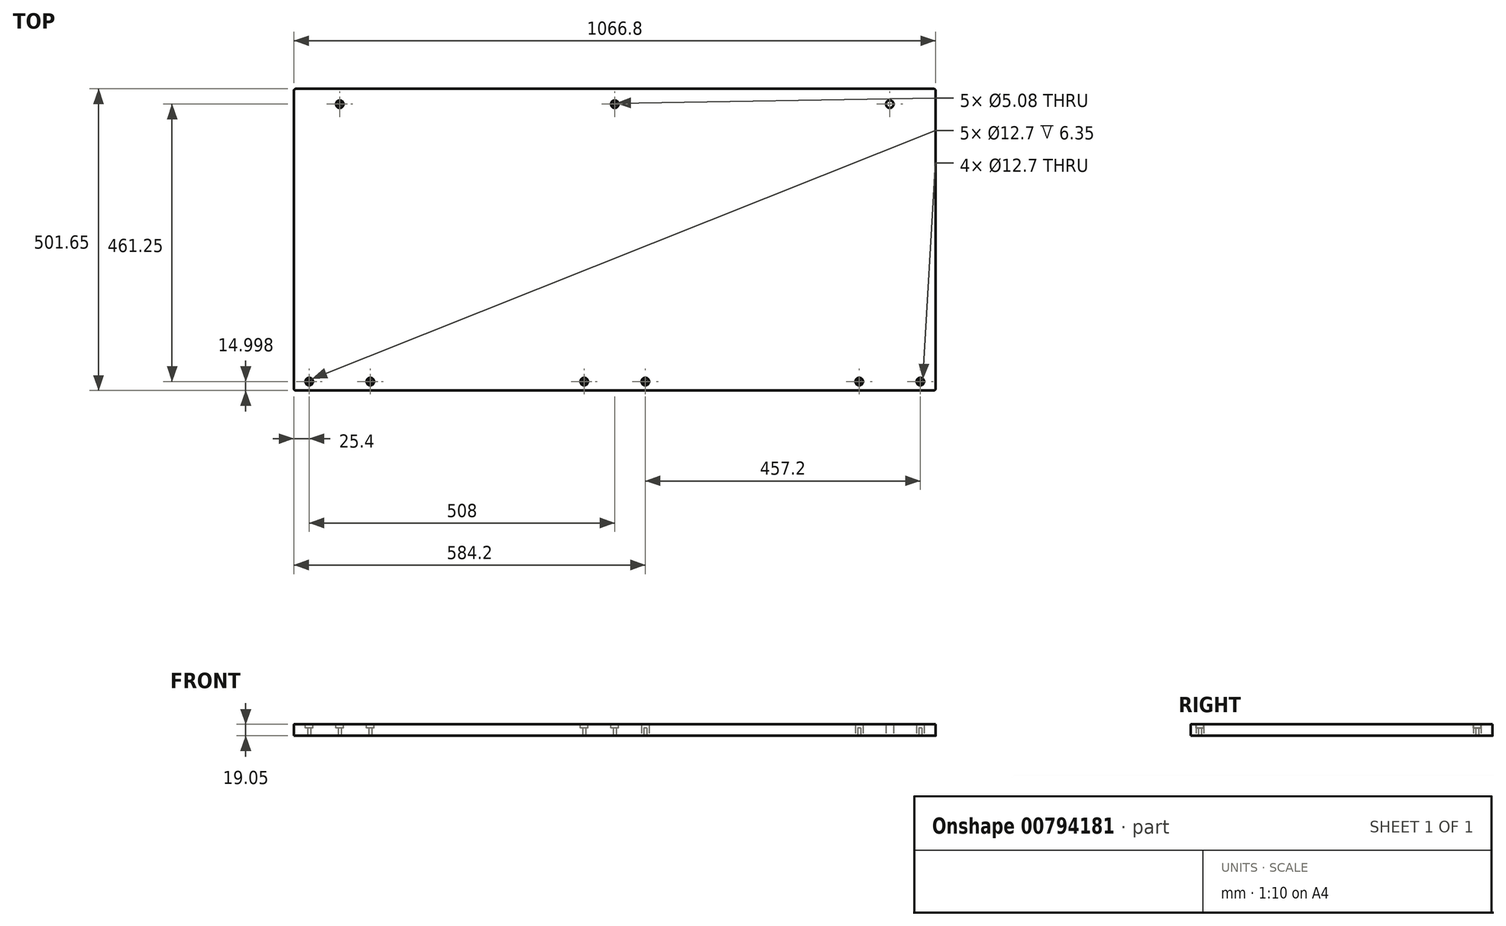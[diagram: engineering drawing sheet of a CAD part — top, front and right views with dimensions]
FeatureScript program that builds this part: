
annotation { "Feature Type Name" : "Feature", "Feature Type Description" : "" }
export const myFeature = defineFeature(function(context is Context, id is Id, definition is map)
    precondition{}
    {
        {
            var Q0;
            Q0=qCreatedBy(makeId("Top.planeOp"),FACE);
            var sketch = newSketch(context, id + "F0", { "sketchPlane" : qUnion([Q0])});
            skFitSpline(sketch, "E0", {"points": [v(-588.01, -204.6) * mm, v(-588.01, -206.35) * mm, v(-586.59, -207.77) * mm, v(-584.84, -207.77) * mm]});
            skFitSpline(sketch, "E1", {"points": [v(475.61, -207.77) * mm, v(477.37, -207.77) * mm, v(478.79, -206.35) * mm, v(478.8, -204.6) * mm]});
            skFitSpline(sketch, "E2", {"points": [v(478.8, 290.7) * mm, v(478.8, 292.46) * mm, v(477.37, 293.88) * mm, v(475.62, 293.88) * mm]});
            skFitSpline(sketch, "E3", {"points": [v(-584.83, 293.88) * mm, v(-586.59, 293.88) * mm, v(-588, 292.46) * mm, v(-588.01, 290.7) * mm]});
            skLineSegment(sketch, "E4", {"start": v(475.49, -207.77) * mm, "end": v(-584.96, -207.77) * mm});
            skLineSegment(sketch, "E5", {"start": v(478.8, 290.58) * mm, "end": v(478.8, -204.72) * mm});
            skLineSegment(sketch, "E6", {"start": v(-584.96, 293.88) * mm, "end": v(475.49, 293.88) * mm});
            skLineSegment(sketch, "E7", {"start": v(-588.01, -204.72) * mm, "end": v(-588.01, 290.58) * mm});
            skLineSegment(sketch, "E8", {"start": v(768.1, -204.72) * mm, "end": v(768.1, -207.77) * mm});
            skLineSegment(sketch, "E9", {"start": v(768.1, 293.88) * mm, "end": v(768.1, 290.58) * mm});
            skLineSegment(sketch, "E10", {"start": v(768.1, -207.77) * mm, "end": v(787.15, -207.77) * mm});
            skLineSegment(sketch, "E11", {"start": v(787.15, -207.77) * mm, "end": v(787.15, -204.72) * mm});
            skLineSegment(sketch, "E12", {"start": v(787.15, 290.58) * mm, "end": v(787.15, 293.88) * mm});
            skLineSegment(sketch, "E13", {"start": v(787.15, 293.88) * mm, "end": v(768.1, 293.88) * mm});
            skLineSegment(sketch, "E14", {"start": v(768.1, 290.58) * mm, "end": v(768.1, -204.72) * mm});
            skLineSegment(sketch, "E15", {"start": v(787.15, 290.58) * mm, "end": v(787.15, -204.72) * mm});
            skLineSegment(sketch, "E16", {"start": v(774.45, -199.14) * mm, "end": v(774.45, -195.07) * mm});
            skLineSegment(sketch, "E17", {"start": v(774.45, -190.75) * mm, "end": v(774.45, -186.44) * mm});
            skLineSegment(sketch, "E18", {"start": v(774.45, 262.13) * mm, "end": v(774.45, 266.2) * mm});
            skLineSegment(sketch, "E19", {"start": v(774.45, 270.51) * mm, "end": v(774.45, 274.83) * mm});
            skLineSegment(sketch, "E20", {"start": v(774.45, -199.14) * mm, "end": v(772.41, -199.14) * mm});
            skLineSegment(sketch, "E21", {"start": v(770.38, -199.14) * mm, "end": v(768.1, -199.14) * mm});
            skLineSegment(sketch, "E22", {"start": v(774.45, -186.44) * mm, "end": v(772.41, -186.44) * mm});
            skLineSegment(sketch, "E23", {"start": v(770.38, -186.44) * mm, "end": v(768.1, -186.44) * mm});
            skLineSegment(sketch, "E24", {"start": v(787.15, -195.33) * mm, "end": v(783.08, -195.33) * mm});
            skLineSegment(sketch, "E25", {"start": v(778.76, -195.33) * mm, "end": v(774.45, -195.33) * mm});
            skLineSegment(sketch, "E26", {"start": v(787.15, -190.25) * mm, "end": v(783.08, -190.25) * mm});
            skLineSegment(sketch, "E27", {"start": v(778.76, -190.25) * mm, "end": v(774.45, -190.25) * mm});
            skLineSegment(sketch, "E28", {"start": v(774.45, 262.13) * mm, "end": v(772.41, 262.13) * mm});
            skLineSegment(sketch, "E29", {"start": v(770.38, 262.13) * mm, "end": v(768.1, 262.13) * mm});
            skLineSegment(sketch, "E30", {"start": v(774.45, 274.83) * mm, "end": v(772.41, 274.83) * mm});
            skLineSegment(sketch, "E31", {"start": v(770.38, 274.83) * mm, "end": v(768.1, 274.83) * mm});
            skLineSegment(sketch, "E32", {"start": v(787.15, 265.94) * mm, "end": v(783.08, 265.94) * mm});
            skLineSegment(sketch, "E33", {"start": v(778.76, 265.94) * mm, "end": v(774.45, 265.94) * mm});
            skLineSegment(sketch, "E34", {"start": v(787.15, 271.02) * mm, "end": v(783.08, 271.02) * mm});
            skLineSegment(sketch, "E35", {"start": v(778.76, 271.02) * mm, "end": v(774.45, 271.02) * mm});
            skLineSegment(sketch, "E36", {"start": v(-1041.4, -812.8) * mm, "end": v(-1041.4, 812.8) * mm});
            skLineSegment(sketch, "E37", {"start": v(-1041.4, 812.8) * mm, "end": v(1041.4, 812.8) * mm});
            skLineSegment(sketch, "E38", {"start": v(1041.4, 812.8) * mm, "end": v(1041.4, -812.8) * mm});
            skLineSegment(sketch, "E39", {"start": v(1041.4, -812.8) * mm, "end": v(-1041.4, -812.8) * mm});
            skLineSegment(sketch, "E40", {"start": v(0, -838.2) * mm, "end": v(0, -812.8) * mm});
            skLineSegment(sketch, "E41", {"start": v(0, -812.8) * mm, "end": v(-8.89, -828.04) * mm});
            skLineSegment(sketch, "E42", {"start": v(-8.89, -828.04) * mm, "end": v(8.89, -828.04) * mm});
            skLineSegment(sketch, "E43", {"start": v(8.89, -828.04) * mm, "end": v(0, -812.8) * mm});
            skLineSegment(sketch, "E44", {"start": v(0, 838.2) * mm, "end": v(0, 812.8) * mm});
            skLineSegment(sketch, "E45", {"start": v(0, 812.8) * mm, "end": v(-8.89, 828.04) * mm});
            skLineSegment(sketch, "E46", {"start": v(-8.89, 828.04) * mm, "end": v(8.89, 828.04) * mm});
            skLineSegment(sketch, "E47", {"start": v(8.89, 828.04) * mm, "end": v(0, 812.8) * mm});
            skLineSegment(sketch, "E48", {"start": v(-1066.8, 0) * mm, "end": v(-1041.4, 0) * mm});
            skLineSegment(sketch, "E49", {"start": v(-1041.4, 0) * mm, "end": v(-1056.64, 8.89) * mm});
            skLineSegment(sketch, "E50", {"start": v(-1056.64, 8.89) * mm, "end": v(-1056.64, -8.89) * mm});
            skLineSegment(sketch, "E51", {"start": v(-1056.64, -8.89) * mm, "end": v(-1041.4, 0) * mm});
            skLineSegment(sketch, "E52", {"start": v(1066.8, 0) * mm, "end": v(1041.4, 0) * mm});
            skLineSegment(sketch, "E53", {"start": v(1041.4, 0) * mm, "end": v(1056.64, 8.89) * mm});
            skLineSegment(sketch, "E54", {"start": v(1056.64, 8.89) * mm, "end": v(1056.64, -8.89) * mm});
            skLineSegment(sketch, "E55", {"start": v(1056.64, -8.89) * mm, "end": v(1041.4, 0) * mm});
            skLineSegment(sketch, "E56", {"start": v(-558.8, -812.8) * mm, "end": v(-558.8, -829.06) * mm});
            skLineSegment(sketch, "E57", {"start": v(-558.8, 812.8) * mm, "end": v(-558.8, 829.06) * mm});
            skLineSegment(sketch, "E58", {"start": v(558.8, -812.8) * mm, "end": v(558.8, -829.06) * mm});
            skLineSegment(sketch, "E59", {"start": v(558.8, 812.8) * mm, "end": v(558.8, 829.06) * mm});
            skLineSegment(sketch, "E60", {"start": v(-834.04, 821.05) * mm, "end": v(-835.49, 821.05) * mm});
            skLineSegment(sketch, "E61", {"start": v(-835.49, 821.05) * mm, "end": v(-835.49, 816.86) * mm});
            skLineSegment(sketch, "E62", {"start": v(-835.49, 816.86) * mm, "end": v(-837.06, 816.86) * mm});
            skLineSegment(sketch, "E63", {"start": v(-837.06, 816.86) * mm, "end": v(-837.06, 821.05) * mm});
            skLineSegment(sketch, "E64", {"start": v(-837.06, 821.05) * mm, "end": v(-842.44, 821.05) * mm});
            skLineSegment(sketch, "E65", {"start": v(-842.44, 821.05) * mm, "end": v(-842.44, 822.77) * mm});
            skLineSegment(sketch, "E66", {"start": v(-842.44, 822.77) * mm, "end": v(-837, 829.05) * mm});
            skLineSegment(sketch, "E67", {"start": v(-837, 829.05) * mm, "end": v(-835.49, 829.05) * mm});
            skLineSegment(sketch, "E68", {"start": v(-835.49, 829.05) * mm, "end": v(-835.49, 822.36) * mm});
            skLineSegment(sketch, "E69", {"start": v(-835.49, 822.36) * mm, "end": v(-834.04, 822.36) * mm});
            skLineSegment(sketch, "E70", {"start": v(-834.04, 822.36) * mm, "end": v(-834.04, 821.05) * mm});
            skLineSegment(sketch, "E71", {"start": v(-837.06, 822.36) * mm, "end": v(-837.06, 827.13) * mm});
            skLineSegment(sketch, "E72", {"start": v(-837.06, 827.13) * mm, "end": v(-841.17, 822.36) * mm});
            skLineSegment(sketch, "E73", {"start": v(-841.17, 822.36) * mm, "end": v(-837.06, 822.36) * mm});
            skLineSegment(sketch, "E74", {"start": v(-834.04, -824.86) * mm, "end": v(-835.49, -824.86) * mm});
            skLineSegment(sketch, "E75", {"start": v(-835.49, -824.86) * mm, "end": v(-835.49, -829.06) * mm});
            skLineSegment(sketch, "E76", {"start": v(-835.49, -829.06) * mm, "end": v(-837.06, -829.06) * mm});
            skLineSegment(sketch, "E77", {"start": v(-837.06, -829.06) * mm, "end": v(-837.06, -824.86) * mm});
            skLineSegment(sketch, "E78", {"start": v(-837.06, -824.86) * mm, "end": v(-842.44, -824.86) * mm});
            skLineSegment(sketch, "E79", {"start": v(-842.44, -824.86) * mm, "end": v(-842.44, -823.15) * mm});
            skLineSegment(sketch, "E80", {"start": v(-842.44, -823.15) * mm, "end": v(-837, -816.87) * mm});
            skLineSegment(sketch, "E81", {"start": v(-837, -816.87) * mm, "end": v(-835.49, -816.87) * mm});
            skLineSegment(sketch, "E82", {"start": v(-835.49, -816.87) * mm, "end": v(-835.49, -823.55) * mm});
            skLineSegment(sketch, "E83", {"start": v(-835.49, -823.55) * mm, "end": v(-834.04, -823.55) * mm});
            skLineSegment(sketch, "E84", {"start": v(-834.04, -823.55) * mm, "end": v(-834.04, -824.86) * mm});
            skLineSegment(sketch, "E85", {"start": v(-837.06, -823.55) * mm, "end": v(-837.06, -818.8) * mm});
            skLineSegment(sketch, "E86", {"start": v(-837.06, -818.8) * mm, "end": v(-841.17, -823.55) * mm});
            skLineSegment(sketch, "E87", {"start": v(-841.17, -823.55) * mm, "end": v(-837.06, -823.55) * mm});
            skLineSegment(sketch, "E88", {"start": v(-1041.4, -431.8) * mm, "end": v(-1057.66, -431.8) * mm});
            skLineSegment(sketch, "E89", {"start": v(1041.4, -431.8) * mm, "end": v(1057.66, -431.8) * mm});
            skLineSegment(sketch, "E90", {"start": v(-1041.4, 431.8) * mm, "end": v(-1057.66, 431.8) * mm});
            skLineSegment(sketch, "E91", {"start": v(1041.4, 431.8) * mm, "end": v(1057.66, 431.8) * mm});
            skLineSegment(sketch, "E92", {"start": v(-1056.72, -653.8) * mm, "end": v(-1052.61, -641.6) * mm});
            skLineSegment(sketch, "E93", {"start": v(-1052.61, -641.6) * mm, "end": v(-1050.62, -641.6) * mm});
            skLineSegment(sketch, "E94", {"start": v(-1050.62, -641.6) * mm, "end": v(-1046.5, -653.8) * mm});
            skLineSegment(sketch, "E95", {"start": v(-1046.5, -653.8) * mm, "end": v(-1048.22, -653.8) * mm});
            skLineSegment(sketch, "E96", {"start": v(-1048.22, -653.8) * mm, "end": v(-1049.32, -650.4) * mm});
            skLineSegment(sketch, "E97", {"start": v(-1049.32, -650.4) * mm, "end": v(-1053.98, -650.4) * mm});
            skLineSegment(sketch, "E98", {"start": v(-1053.98, -650.4) * mm, "end": v(-1055.08, -653.8) * mm});
            skLineSegment(sketch, "E99", {"start": v(-1055.08, -653.8) * mm, "end": v(-1056.72, -653.8) * mm});
            skLineSegment(sketch, "E100", {"start": v(-1049.77, -649) * mm, "end": v(-1051.65, -643.26) * mm});
            skLineSegment(sketch, "E101", {"start": v(-1051.65, -643.26) * mm, "end": v(-1053.53, -649) * mm});
            skLineSegment(sketch, "E102", {"start": v(-1053.53, -649) * mm, "end": v(-1049.77, -649) * mm});
            skLineSegment(sketch, "E103", {"start": v(1046.4, -653.8) * mm, "end": v(1050.5, -641.6) * mm});
            skLineSegment(sketch, "E104", {"start": v(1050.5, -641.6) * mm, "end": v(1052.5, -641.6) * mm});
            skLineSegment(sketch, "E105", {"start": v(1052.5, -641.6) * mm, "end": v(1056.61, -653.8) * mm});
            skLineSegment(sketch, "E106", {"start": v(1056.61, -653.8) * mm, "end": v(1054.9, -653.8) * mm});
            skLineSegment(sketch, "E107", {"start": v(1054.9, -653.8) * mm, "end": v(1053.8, -650.4) * mm});
            skLineSegment(sketch, "E108", {"start": v(1053.8, -650.4) * mm, "end": v(1049.14, -650.4) * mm});
            skLineSegment(sketch, "E109", {"start": v(1049.14, -650.4) * mm, "end": v(1048.03, -653.8) * mm});
            skLineSegment(sketch, "E110", {"start": v(1048.03, -653.8) * mm, "end": v(1046.4, -653.8) * mm});
            skLineSegment(sketch, "E111", {"start": v(1053.35, -649) * mm, "end": v(1051.46, -643.26) * mm});
            skLineSegment(sketch, "E112", {"start": v(1051.46, -643.26) * mm, "end": v(1049.6, -649) * mm});
            skLineSegment(sketch, "E113", {"start": v(1049.6, -649) * mm, "end": v(1053.35, -649) * mm});
            skLineSegment(sketch, "E114", {"start": v(254, -596.9) * mm, "end": v(533.4, -596.9) * mm});
            skLineSegment(sketch, "E115", {"start": v(254, -635) * mm, "end": v(533.4, -635) * mm});
            skLineSegment(sketch, "E116", {"start": v(254, -673.1) * mm, "end": v(533.4, -673.1) * mm});
            skLineSegment(sketch, "E117", {"start": v(254, -711.2) * mm, "end": v(533.4, -711.2) * mm});
            skLineSegment(sketch, "E118", {"start": v(254, -749.3) * mm, "end": v(533.4, -749.3) * mm});
            skLineSegment(sketch, "E119", {"start": v(431.8, -812.8) * mm, "end": v(431.8, -558.8) * mm});
            skLineSegment(sketch, "E120", {"start": v(990.6, -787.4) * mm, "end": v(990.6, -736.6) * mm});
            skLineSegment(sketch, "E121", {"start": v(838.2, -787.4) * mm, "end": v(838.2, -812.8) * mm});
            skLineSegment(sketch, "E122", {"start": v(685.8, -787.4) * mm, "end": v(685.8, -736.6) * mm});
            skLineSegment(sketch, "E123", {"start": v(647.2, -787.4) * mm, "end": v(647.2, -812.8) * mm});
            skLineSegment(sketch, "E124", {"start": v(584.2, -787.4) * mm, "end": v(584.2, -736.6) * mm});
            skLineSegment(sketch, "E125", {"start": v(1041.4, -787.4) * mm, "end": v(533.4, -787.4) * mm});
            skLineSegment(sketch, "E126", {"start": v(533.4, -787.4) * mm, "end": v(254, -787.4) * mm});
            skLineSegment(sketch, "E127", {"start": v(1041.4, -736.6) * mm, "end": v(533.4, -736.6) * mm});
            skLineSegment(sketch, "E128", {"start": v(533.4, -621.8) * mm, "end": v(1041.4, -621.8) * mm});
            skLineSegment(sketch, "E129", {"start": v(533.4, -812.8) * mm, "end": v(533.4, -558.8) * mm});
            skLineSegment(sketch, "E130", {"start": v(254, -812.8) * mm, "end": v(1041.4, -812.8) * mm});
            skLineSegment(sketch, "E131", {"start": v(1041.4, -812.8) * mm, "end": v(1041.4, -558.8) * mm});
            skLineSegment(sketch, "E132", {"start": v(1041.4, -558.8) * mm, "end": v(254, -558.8) * mm});
            skLineSegment(sketch, "E133", {"start": v(254, -558.8) * mm, "end": v(254, -812.8) * mm});
            skLineSegment(sketch, "E134", {"start": v(857.53, -809.5) * mm, "end": v(856.18, -809.5) * mm});
            skLineSegment(sketch, "E135", {"start": v(856.18, -809.5) * mm, "end": v(856.18, -804.53) * mm});
            skLineSegment(sketch, "E136", {"start": v(856.18, -804.53) * mm, "end": v(851.5, -804.53) * mm});
            skLineSegment(sketch, "E137", {"start": v(851.5, -804.53) * mm, "end": v(851.5, -809.5) * mm});
            skLineSegment(sketch, "E138", {"start": v(851.5, -809.5) * mm, "end": v(850.15, -809.5) * mm});
            skLineSegment(sketch, "E139", {"start": v(850.15, -809.5) * mm, "end": v(850.15, -799.34) * mm});
            skLineSegment(sketch, "E140", {"start": v(850.15, -799.34) * mm, "end": v(851.5, -799.34) * mm});
            skLineSegment(sketch, "E141", {"start": v(851.5, -799.34) * mm, "end": v(851.5, -803.32) * mm});
            skLineSegment(sketch, "E142", {"start": v(851.5, -803.32) * mm, "end": v(856.18, -803.32) * mm});
            skLineSegment(sketch, "E143", {"start": v(856.18, -803.32) * mm, "end": v(856.18, -799.34) * mm});
            skLineSegment(sketch, "E144", {"start": v(856.18, -799.34) * mm, "end": v(857.53, -799.34) * mm});
            skLineSegment(sketch, "E145", {"start": v(857.53, -799.34) * mm, "end": v(857.53, -809.5) * mm});
            skLineSegment(sketch, "E146", {"start": v(859.55, -809.5) * mm, "end": v(859.55, -799.34) * mm});
            skLineSegment(sketch, "E147", {"start": v(859.55, -799.34) * mm, "end": v(865.9, -799.34) * mm});
            skLineSegment(sketch, "E148", {"start": v(865.9, -799.34) * mm, "end": v(865.9, -800.54) * mm});
            skLineSegment(sketch, "E149", {"start": v(865.9, -800.54) * mm, "end": v(860.9, -800.54) * mm});
            skLineSegment(sketch, "E150", {"start": v(860.9, -800.54) * mm, "end": v(860.9, -803.32) * mm});
            skLineSegment(sketch, "E151", {"start": v(860.9, -803.32) * mm, "end": v(865.56, -803.32) * mm});
            skLineSegment(sketch, "E152", {"start": v(865.56, -803.32) * mm, "end": v(865.56, -804.53) * mm});
            skLineSegment(sketch, "E153", {"start": v(865.56, -804.53) * mm, "end": v(860.9, -804.53) * mm});
            skLineSegment(sketch, "E154", {"start": v(860.9, -804.53) * mm, "end": v(860.9, -808.3) * mm});
            skLineSegment(sketch, "E155", {"start": v(860.9, -808.3) * mm, "end": v(865.9, -808.3) * mm});
            skLineSegment(sketch, "E156", {"start": v(865.9, -808.3) * mm, "end": v(865.9, -809.5) * mm});
            skLineSegment(sketch, "E157", {"start": v(865.9, -809.5) * mm, "end": v(859.55, -809.5) * mm});
            skLineSegment(sketch, "E158", {"start": v(867.42, -809.5) * mm, "end": v(867.42, -799.34) * mm});
            skLineSegment(sketch, "E159", {"start": v(867.42, -799.34) * mm, "end": v(873.78, -799.34) * mm});
            skLineSegment(sketch, "E160", {"start": v(873.78, -799.34) * mm, "end": v(873.78, -800.54) * mm});
            skLineSegment(sketch, "E161", {"start": v(873.78, -800.54) * mm, "end": v(868.78, -800.54) * mm});
            skLineSegment(sketch, "E162", {"start": v(868.78, -800.54) * mm, "end": v(868.78, -803.32) * mm});
            skLineSegment(sketch, "E163", {"start": v(868.78, -803.32) * mm, "end": v(873.43, -803.32) * mm});
            skLineSegment(sketch, "E164", {"start": v(873.43, -803.32) * mm, "end": v(873.43, -804.53) * mm});
            skLineSegment(sketch, "E165", {"start": v(873.43, -804.53) * mm, "end": v(868.78, -804.53) * mm});
            skLineSegment(sketch, "E166", {"start": v(868.78, -804.53) * mm, "end": v(868.78, -808.3) * mm});
            skLineSegment(sketch, "E167", {"start": v(868.78, -808.3) * mm, "end": v(873.78, -808.3) * mm});
            skLineSegment(sketch, "E168", {"start": v(873.78, -808.3) * mm, "end": v(873.78, -809.5) * mm});
            skLineSegment(sketch, "E169", {"start": v(873.78, -809.5) * mm, "end": v(867.42, -809.5) * mm});
            skLineSegment(sketch, "E170", {"start": v(877.42, -809.5) * mm, "end": v(877.42, -800.54) * mm});
            skLineSegment(sketch, "E171", {"start": v(877.42, -800.54) * mm, "end": v(874, -800.54) * mm});
            skLineSegment(sketch, "E172", {"start": v(874, -800.54) * mm, "end": v(874, -799.34) * mm});
            skLineSegment(sketch, "E173", {"start": v(874, -799.34) * mm, "end": v(882.18, -799.34) * mm});
            skLineSegment(sketch, "E174", {"start": v(882.18, -799.34) * mm, "end": v(882.18, -800.54) * mm});
            skLineSegment(sketch, "E175", {"start": v(882.18, -800.54) * mm, "end": v(878.77, -800.54) * mm});
            skLineSegment(sketch, "E176", {"start": v(878.77, -800.54) * mm, "end": v(878.77, -809.5) * mm});
            skLineSegment(sketch, "E177", {"start": v(878.77, -809.5) * mm, "end": v(877.42, -809.5) * mm});
            skLineSegment(sketch, "E178", {"start": v(924.05, -800.54) * mm, "end": v(919.32, -800.54) * mm});
            skLineSegment(sketch, "E179", {"start": v(919.32, -800.54) * mm, "end": v(919.32, -803.4) * mm});
            skLineSegment(sketch, "E180", {"start": v(919.32, -803.4) * mm, "end": v(923.85, -803.4) * mm});
            skLineSegment(sketch, "E181", {"start": v(923.85, -803.4) * mm, "end": v(923.85, -804.6) * mm});
            skLineSegment(sketch, "E182", {"start": v(923.85, -804.6) * mm, "end": v(919.32, -804.6) * mm});
            skLineSegment(sketch, "E183", {"start": v(919.32, -804.6) * mm, "end": v(919.32, -809.5) * mm});
            skLineSegment(sketch, "E184", {"start": v(919.32, -809.5) * mm, "end": v(917.97, -809.5) * mm});
            skLineSegment(sketch, "E185", {"start": v(917.97, -809.5) * mm, "end": v(917.97, -799.34) * mm});
            skLineSegment(sketch, "E186", {"start": v(917.97, -799.34) * mm, "end": v(924.05, -799.34) * mm});
            skLineSegment(sketch, "E187", {"start": v(924.05, -799.34) * mm, "end": v(924.05, -800.54) * mm});
            skLineSegment(sketch, "E188", {"start": v(275.01, -572) * mm, "end": v(278.44, -561.85) * mm});
            skLineSegment(sketch, "E189", {"start": v(278.44, -561.85) * mm, "end": v(280.1, -561.85) * mm});
            skLineSegment(sketch, "E190", {"start": v(280.1, -561.85) * mm, "end": v(283.53, -572) * mm});
            skLineSegment(sketch, "E191", {"start": v(283.53, -572) * mm, "end": v(282.1, -572) * mm});
            skLineSegment(sketch, "E192", {"start": v(282.1, -572) * mm, "end": v(281.18, -569.17) * mm});
            skLineSegment(sketch, "E193", {"start": v(281.18, -569.17) * mm, "end": v(277.3, -569.17) * mm});
            skLineSegment(sketch, "E194", {"start": v(277.3, -569.17) * mm, "end": v(276.38, -572) * mm});
            skLineSegment(sketch, "E195", {"start": v(276.38, -572) * mm, "end": v(275.01, -572) * mm});
            skLineSegment(sketch, "E196", {"start": v(280.8, -568.02) * mm, "end": v(279.24, -563.23) * mm});
            skLineSegment(sketch, "E197", {"start": v(279.24, -563.23) * mm, "end": v(277.67, -568.02) * mm});
            skLineSegment(sketch, "E198", {"start": v(277.67, -568.02) * mm, "end": v(280.8, -568.02) * mm});
            skLineSegment(sketch, "E199", {"start": v(295.89, -561.85) * mm, "end": v(293.33, -572) * mm});
            skLineSegment(sketch, "E200", {"start": v(293.33, -572) * mm, "end": v(291.81, -572) * mm});
            skLineSegment(sketch, "E201", {"start": v(291.81, -572) * mm, "end": v(289.75, -563.58) * mm});
            skLineSegment(sketch, "E202", {"start": v(289.75, -563.58) * mm, "end": v(287.73, -572) * mm});
            skLineSegment(sketch, "E203", {"start": v(287.73, -572) * mm, "end": v(286.24, -572) * mm});
            skLineSegment(sketch, "E204", {"start": v(286.24, -572) * mm, "end": v(283.64, -561.85) * mm});
            skLineSegment(sketch, "E205", {"start": v(283.64, -561.85) * mm, "end": v(285.03, -561.85) * mm});
            skLineSegment(sketch, "E206", {"start": v(285.03, -561.85) * mm, "end": v(287.07, -570.3) * mm});
            skLineSegment(sketch, "E207", {"start": v(287.07, -570.3) * mm, "end": v(289.1, -561.85) * mm});
            skLineSegment(sketch, "E208", {"start": v(289.1, -561.85) * mm, "end": v(290.48, -561.85) * mm});
            skLineSegment(sketch, "E209", {"start": v(290.48, -561.85) * mm, "end": v(292.53, -570.38) * mm});
            skLineSegment(sketch, "E210", {"start": v(292.53, -570.38) * mm, "end": v(294.56, -561.85) * mm});
            skLineSegment(sketch, "E211", {"start": v(294.56, -561.85) * mm, "end": v(295.89, -561.85) * mm});
            skLineSegment(sketch, "E212", {"start": v(304.46, -572) * mm, "end": v(302.94, -572) * mm});
            skLineSegment(sketch, "E213", {"start": v(302.94, -572) * mm, "end": v(298.46, -563.25) * mm});
            skLineSegment(sketch, "E214", {"start": v(298.46, -563.25) * mm, "end": v(298.46, -572) * mm});
            skLineSegment(sketch, "E215", {"start": v(298.46, -572) * mm, "end": v(297.2, -572) * mm});
            skLineSegment(sketch, "E216", {"start": v(297.2, -572) * mm, "end": v(297.2, -561.85) * mm});
            skLineSegment(sketch, "E217", {"start": v(297.2, -561.85) * mm, "end": v(299.11, -561.85) * mm});
            skLineSegment(sketch, "E218", {"start": v(299.11, -561.85) * mm, "end": v(303.2, -569.9) * mm});
            skLineSegment(sketch, "E219", {"start": v(303.2, -569.9) * mm, "end": v(303.2, -561.85) * mm});
            skLineSegment(sketch, "E220", {"start": v(303.2, -561.85) * mm, "end": v(304.46, -561.85) * mm});
            skLineSegment(sketch, "E221", {"start": v(304.46, -561.85) * mm, "end": v(304.46, -572) * mm});
            skLineSegment(sketch, "E222", {"start": v(273.83, -610.36) * mm, "end": v(272.48, -610.36) * mm});
            skLineSegment(sketch, "E223", {"start": v(272.48, -610.36) * mm, "end": v(272.48, -605.39) * mm});
            skLineSegment(sketch, "E224", {"start": v(272.48, -605.39) * mm, "end": v(267.81, -605.39) * mm});
            skLineSegment(sketch, "E225", {"start": v(267.81, -605.39) * mm, "end": v(267.81, -610.36) * mm});
            skLineSegment(sketch, "E226", {"start": v(267.81, -610.36) * mm, "end": v(266.46, -610.36) * mm});
            skLineSegment(sketch, "E227", {"start": v(266.46, -610.36) * mm, "end": v(266.46, -600.2) * mm});
            skLineSegment(sketch, "E228", {"start": v(266.46, -600.2) * mm, "end": v(267.81, -600.2) * mm});
            skLineSegment(sketch, "E229", {"start": v(267.81, -600.2) * mm, "end": v(267.81, -604.19) * mm});
            skLineSegment(sketch, "E230", {"start": v(267.81, -604.19) * mm, "end": v(272.48, -604.19) * mm});
            skLineSegment(sketch, "E231", {"start": v(272.48, -604.19) * mm, "end": v(272.48, -600.2) * mm});
            skLineSegment(sketch, "E232", {"start": v(272.48, -600.2) * mm, "end": v(273.83, -600.2) * mm});
            skLineSegment(sketch, "E233", {"start": v(273.83, -600.2) * mm, "end": v(273.83, -610.36) * mm});
            skLineSegment(sketch, "E234", {"start": v(275.86, -610.36) * mm, "end": v(275.86, -600.2) * mm});
            skLineSegment(sketch, "E235", {"start": v(275.86, -600.2) * mm, "end": v(282.2, -600.2) * mm});
            skLineSegment(sketch, "E236", {"start": v(282.2, -600.2) * mm, "end": v(282.2, -601.4) * mm});
            skLineSegment(sketch, "E237", {"start": v(282.2, -601.4) * mm, "end": v(277.2, -601.4) * mm});
            skLineSegment(sketch, "E238", {"start": v(277.2, -601.4) * mm, "end": v(277.2, -604.19) * mm});
            skLineSegment(sketch, "E239", {"start": v(277.2, -604.19) * mm, "end": v(281.87, -604.19) * mm});
            skLineSegment(sketch, "E240", {"start": v(281.87, -604.19) * mm, "end": v(281.87, -605.39) * mm});
            skLineSegment(sketch, "E241", {"start": v(281.87, -605.39) * mm, "end": v(277.2, -605.39) * mm});
            skLineSegment(sketch, "E242", {"start": v(277.2, -605.39) * mm, "end": v(277.2, -609.16) * mm});
            skLineSegment(sketch, "E243", {"start": v(277.2, -609.16) * mm, "end": v(282.2, -609.16) * mm});
            skLineSegment(sketch, "E244", {"start": v(282.2, -609.16) * mm, "end": v(282.2, -610.36) * mm});
            skLineSegment(sketch, "E245", {"start": v(282.2, -610.36) * mm, "end": v(275.86, -610.36) * mm});
            skLineSegment(sketch, "E246", {"start": v(299.52, -610.36) * mm, "end": v(297.76, -610.36) * mm});
            skLineSegment(sketch, "E247", {"start": v(297.76, -610.36) * mm, "end": v(294.06, -605.64) * mm});
            skLineSegment(sketch, "E248", {"start": v(294.06, -605.64) * mm, "end": v(293.46, -606.3) * mm});
            skLineSegment(sketch, "E249", {"start": v(293.46, -606.3) * mm, "end": v(293.46, -610.36) * mm});
            skLineSegment(sketch, "E250", {"start": v(293.46, -610.36) * mm, "end": v(292.11, -610.36) * mm});
            skLineSegment(sketch, "E251", {"start": v(292.11, -610.36) * mm, "end": v(292.11, -600.2) * mm});
            skLineSegment(sketch, "E252", {"start": v(292.11, -600.2) * mm, "end": v(293.46, -600.2) * mm});
            skLineSegment(sketch, "E253", {"start": v(293.46, -600.2) * mm, "end": v(293.46, -604.88) * mm});
            skLineSegment(sketch, "E254", {"start": v(293.46, -604.88) * mm, "end": v(297.63, -600.2) * mm});
            skLineSegment(sketch, "E255", {"start": v(297.63, -600.2) * mm, "end": v(299.27, -600.2) * mm});
            skLineSegment(sketch, "E256", {"start": v(299.27, -600.2) * mm, "end": v(295.07, -604.74) * mm});
            skLineSegment(sketch, "E257", {"start": v(295.07, -604.74) * mm, "end": v(299.52, -610.36) * mm});
            skLineSegment(sketch, "E258", {"start": v(300.24, -610.36) * mm, "end": v(300.24, -600.2) * mm});
            skLineSegment(sketch, "E259", {"start": v(300.24, -600.2) * mm, "end": v(306.6, -600.2) * mm});
            skLineSegment(sketch, "E260", {"start": v(306.6, -600.2) * mm, "end": v(306.6, -601.4) * mm});
            skLineSegment(sketch, "E261", {"start": v(306.6, -601.4) * mm, "end": v(301.6, -601.4) * mm});
            skLineSegment(sketch, "E262", {"start": v(301.6, -601.4) * mm, "end": v(301.6, -604.19) * mm});
            skLineSegment(sketch, "E263", {"start": v(301.6, -604.19) * mm, "end": v(306.25, -604.19) * mm});
            skLineSegment(sketch, "E264", {"start": v(306.25, -604.19) * mm, "end": v(306.25, -605.39) * mm});
            skLineSegment(sketch, "E265", {"start": v(306.25, -605.39) * mm, "end": v(301.6, -605.39) * mm});
            skLineSegment(sketch, "E266", {"start": v(301.6, -605.39) * mm, "end": v(301.6, -609.16) * mm});
            skLineSegment(sketch, "E267", {"start": v(301.6, -609.16) * mm, "end": v(306.6, -609.16) * mm});
            skLineSegment(sketch, "E268", {"start": v(306.6, -609.16) * mm, "end": v(306.6, -610.36) * mm});
            skLineSegment(sketch, "E269", {"start": v(306.6, -610.36) * mm, "end": v(300.24, -610.36) * mm});
            skLineSegment(sketch, "E270", {"start": v(266.89, -648.46) * mm, "end": v(270.3, -638.3) * mm});
            skLineSegment(sketch, "E271", {"start": v(270.3, -638.3) * mm, "end": v(271.97, -638.3) * mm});
            skLineSegment(sketch, "E272", {"start": v(271.97, -638.3) * mm, "end": v(275.4, -648.46) * mm});
            skLineSegment(sketch, "E273", {"start": v(275.4, -648.46) * mm, "end": v(273.97, -648.46) * mm});
            skLineSegment(sketch, "E274", {"start": v(273.97, -648.46) * mm, "end": v(273.05, -645.62) * mm});
            skLineSegment(sketch, "E275", {"start": v(273.05, -645.62) * mm, "end": v(269.17, -645.62) * mm});
            skLineSegment(sketch, "E276", {"start": v(269.17, -645.62) * mm, "end": v(268.25, -648.46) * mm});
            skLineSegment(sketch, "E277", {"start": v(268.25, -648.46) * mm, "end": v(266.89, -648.46) * mm});
            skLineSegment(sketch, "E278", {"start": v(272.68, -644.47) * mm, "end": v(271.1, -639.68) * mm});
            skLineSegment(sketch, "E279", {"start": v(271.1, -639.68) * mm, "end": v(269.55, -644.47) * mm});
            skLineSegment(sketch, "E280", {"start": v(269.55, -644.47) * mm, "end": v(272.68, -644.47) * mm});
            skLineSegment(sketch, "E281", {"start": v(266.78, -686.56) * mm, "end": v(265.43, -686.56) * mm});
            skLineSegment(sketch, "E282", {"start": v(265.43, -686.56) * mm, "end": v(265.43, -677.81) * mm});
            skLineSegment(sketch, "E283", {"start": v(265.43, -677.81) * mm, "end": v(262.78, -683.77) * mm});
            skLineSegment(sketch, "E284", {"start": v(262.78, -683.77) * mm, "end": v(261.97, -683.77) * mm});
            skLineSegment(sketch, "E285", {"start": v(261.97, -683.77) * mm, "end": v(259.34, -677.81) * mm});
            skLineSegment(sketch, "E286", {"start": v(259.34, -677.81) * mm, "end": v(259.34, -686.56) * mm});
            skLineSegment(sketch, "E287", {"start": v(259.34, -686.56) * mm, "end": v(258.08, -686.56) * mm});
            skLineSegment(sketch, "E288", {"start": v(258.08, -686.56) * mm, "end": v(258.08, -676.4) * mm});
            skLineSegment(sketch, "E289", {"start": v(258.08, -676.4) * mm, "end": v(259.92, -676.4) * mm});
            skLineSegment(sketch, "E290", {"start": v(259.92, -676.4) * mm, "end": v(262.46, -682.06) * mm});
            skLineSegment(sketch, "E291", {"start": v(262.46, -682.06) * mm, "end": v(264.9, -676.4) * mm});
            skLineSegment(sketch, "E292", {"start": v(264.9, -676.4) * mm, "end": v(266.78, -676.4) * mm});
            skLineSegment(sketch, "E293", {"start": v(266.78, -676.4) * mm, "end": v(266.78, -686.56) * mm});
            skLineSegment(sketch, "E294", {"start": v(274.82, -677.6) * mm, "end": v(270.1, -677.6) * mm});
            skLineSegment(sketch, "E295", {"start": v(270.1, -677.6) * mm, "end": v(270.1, -680.47) * mm});
            skLineSegment(sketch, "E296", {"start": v(270.1, -680.47) * mm, "end": v(274.63, -680.47) * mm});
            skLineSegment(sketch, "E297", {"start": v(274.63, -680.47) * mm, "end": v(274.63, -681.67) * mm});
            skLineSegment(sketch, "E298", {"start": v(274.63, -681.67) * mm, "end": v(270.1, -681.67) * mm});
            skLineSegment(sketch, "E299", {"start": v(270.1, -681.67) * mm, "end": v(270.1, -686.56) * mm});
            skLineSegment(sketch, "E300", {"start": v(270.1, -686.56) * mm, "end": v(268.75, -686.56) * mm});
            skLineSegment(sketch, "E301", {"start": v(268.75, -686.56) * mm, "end": v(268.75, -676.4) * mm});
            skLineSegment(sketch, "E302", {"start": v(268.75, -676.4) * mm, "end": v(274.82, -676.4) * mm});
            skLineSegment(sketch, "E303", {"start": v(274.82, -676.4) * mm, "end": v(274.82, -677.6) * mm});
            skLineSegment(sketch, "E304", {"start": v(256.98, -724.66) * mm, "end": v(260.4, -714.5) * mm});
            skLineSegment(sketch, "E305", {"start": v(260.4, -714.5) * mm, "end": v(262.07, -714.5) * mm});
            skLineSegment(sketch, "E306", {"start": v(262.07, -714.5) * mm, "end": v(265.5, -724.66) * mm});
            skLineSegment(sketch, "E307", {"start": v(265.5, -724.66) * mm, "end": v(264.07, -724.66) * mm});
            skLineSegment(sketch, "E308", {"start": v(264.07, -724.66) * mm, "end": v(263.15, -721.82) * mm});
            skLineSegment(sketch, "E309", {"start": v(263.15, -721.82) * mm, "end": v(259.27, -721.82) * mm});
            skLineSegment(sketch, "E310", {"start": v(259.27, -721.82) * mm, "end": v(258.34, -724.66) * mm});
            skLineSegment(sketch, "E311", {"start": v(258.34, -724.66) * mm, "end": v(256.98, -724.66) * mm});
            skLineSegment(sketch, "E312", {"start": v(262.77, -720.67) * mm, "end": v(261.2, -715.88) * mm});
            skLineSegment(sketch, "E313", {"start": v(261.2, -715.88) * mm, "end": v(259.64, -720.67) * mm});
            skLineSegment(sketch, "E314", {"start": v(259.64, -720.67) * mm, "end": v(262.77, -720.67) * mm});
            skLineSegment(sketch, "E315", {"start": v(307.86, -714.5) * mm, "end": v(304.36, -724.66) * mm});
            skLineSegment(sketch, "E316", {"start": v(304.36, -724.66) * mm, "end": v(302.9, -724.66) * mm});
            skLineSegment(sketch, "E317", {"start": v(302.9, -724.66) * mm, "end": v(299.41, -714.5) * mm});
            skLineSegment(sketch, "E318", {"start": v(299.41, -714.5) * mm, "end": v(300.86, -714.5) * mm});
            skLineSegment(sketch, "E319", {"start": v(300.86, -714.5) * mm, "end": v(303.67, -722.94) * mm});
            skLineSegment(sketch, "E320", {"start": v(303.67, -722.94) * mm, "end": v(306.48, -714.5) * mm});
            skLineSegment(sketch, "E321", {"start": v(306.48, -714.5) * mm, "end": v(307.86, -714.5) * mm});
            skLineSegment(sketch, "E322", {"start": v(308.88, -724.66) * mm, "end": v(308.88, -714.5) * mm});
            skLineSegment(sketch, "E323", {"start": v(308.88, -714.5) * mm, "end": v(315.23, -714.5) * mm});
            skLineSegment(sketch, "E324", {"start": v(315.23, -714.5) * mm, "end": v(315.23, -715.7) * mm});
            skLineSegment(sketch, "E325", {"start": v(315.23, -715.7) * mm, "end": v(310.23, -715.7) * mm});
            skLineSegment(sketch, "E326", {"start": v(310.23, -715.7) * mm, "end": v(310.23, -718.49) * mm});
            skLineSegment(sketch, "E327", {"start": v(310.23, -718.49) * mm, "end": v(314.89, -718.49) * mm});
            skLineSegment(sketch, "E328", {"start": v(314.89, -718.49) * mm, "end": v(314.89, -719.69) * mm});
            skLineSegment(sketch, "E329", {"start": v(314.89, -719.69) * mm, "end": v(310.23, -719.69) * mm});
            skLineSegment(sketch, "E330", {"start": v(310.23, -719.69) * mm, "end": v(310.23, -723.46) * mm});
            skLineSegment(sketch, "E331", {"start": v(310.23, -723.46) * mm, "end": v(315.23, -723.46) * mm});
            skLineSegment(sketch, "E332", {"start": v(315.23, -723.46) * mm, "end": v(315.23, -724.66) * mm});
            skLineSegment(sketch, "E333", {"start": v(315.23, -724.66) * mm, "end": v(308.88, -724.66) * mm});
            skLineSegment(sketch, "E334", {"start": v(258.34, -593.6) * mm, "end": v(258.34, -580.86) * mm});
            skLineSegment(sketch, "E335", {"start": v(258.34, -580.86) * mm, "end": v(266.3, -580.86) * mm});
            skLineSegment(sketch, "E336", {"start": v(266.3, -580.86) * mm, "end": v(266.3, -582.36) * mm});
            skLineSegment(sketch, "E337", {"start": v(266.3, -582.36) * mm, "end": v(260.03, -582.36) * mm});
            skLineSegment(sketch, "E338", {"start": v(260.03, -582.36) * mm, "end": v(260.03, -585.85) * mm});
            skLineSegment(sketch, "E339", {"start": v(260.03, -585.85) * mm, "end": v(265.88, -585.85) * mm});
            skLineSegment(sketch, "E340", {"start": v(265.88, -585.85) * mm, "end": v(265.88, -587.36) * mm});
            skLineSegment(sketch, "E341", {"start": v(265.88, -587.36) * mm, "end": v(260.03, -587.36) * mm});
            skLineSegment(sketch, "E342", {"start": v(260.03, -587.36) * mm, "end": v(260.03, -592.1) * mm});
            skLineSegment(sketch, "E343", {"start": v(260.03, -592.1) * mm, "end": v(266.3, -592.1) * mm});
            skLineSegment(sketch, "E344", {"start": v(266.3, -592.1) * mm, "end": v(266.3, -593.6) * mm});
            skLineSegment(sketch, "E345", {"start": v(266.3, -593.6) * mm, "end": v(258.34, -593.6) * mm});
            skLineSegment(sketch, "E346", {"start": v(289.36, -584.04) * mm, "end": v(286.93, -593.6) * mm});
            skLineSegment(sketch, "E347", {"start": v(286.93, -593.6) * mm, "end": v(285.45, -593.6) * mm});
            skLineSegment(sketch, "E348", {"start": v(285.45, -593.6) * mm, "end": v(283.1, -586.23) * mm});
            skLineSegment(sketch, "E349", {"start": v(283.1, -586.23) * mm, "end": v(280.8, -593.6) * mm});
            skLineSegment(sketch, "E350", {"start": v(280.8, -593.6) * mm, "end": v(279.3, -593.6) * mm});
            skLineSegment(sketch, "E351", {"start": v(279.3, -593.6) * mm, "end": v(276.86, -584.04) * mm});
            skLineSegment(sketch, "E352", {"start": v(276.86, -584.04) * mm, "end": v(278.54, -584.04) * mm});
            skLineSegment(sketch, "E353", {"start": v(278.54, -584.04) * mm, "end": v(280.23, -591.44) * mm});
            skLineSegment(sketch, "E354", {"start": v(280.23, -591.44) * mm, "end": v(282.5, -584.04) * mm});
            skLineSegment(sketch, "E355", {"start": v(282.5, -584.04) * mm, "end": v(283.82, -584.04) * mm});
            skLineSegment(sketch, "E356", {"start": v(283.82, -584.04) * mm, "end": v(286.15, -591.44) * mm});
            skLineSegment(sketch, "E357", {"start": v(286.15, -591.44) * mm, "end": v(287.74, -584.04) * mm});
            skLineSegment(sketch, "E358", {"start": v(287.74, -584.04) * mm, "end": v(289.36, -584.04) * mm});
            skLineSegment(sketch, "E359", {"start": v(450.73, -577.74) * mm, "end": v(445.74, -593.83) * mm});
            skLineSegment(sketch, "E360", {"start": v(445.74, -593.83) * mm, "end": v(444.3, -593.83) * mm});
            skLineSegment(sketch, "E361", {"start": v(444.3, -593.83) * mm, "end": v(449.26, -577.74) * mm});
            skLineSegment(sketch, "E362", {"start": v(449.26, -577.74) * mm, "end": v(450.73, -577.74) * mm});
            skLineSegment(sketch, "E363", {"start": v(466.73, -577.74) * mm, "end": v(461.74, -593.83) * mm});
            skLineSegment(sketch, "E364", {"start": v(461.74, -593.83) * mm, "end": v(460.3, -593.83) * mm});
            skLineSegment(sketch, "E365", {"start": v(460.3, -593.83) * mm, "end": v(465.26, -577.74) * mm});
            skLineSegment(sketch, "E366", {"start": v(465.26, -577.74) * mm, "end": v(466.73, -577.74) * mm});
            skLineSegment(sketch, "E367", {"start": v(710.67, -739.9) * mm, "end": v(708.12, -750.06) * mm});
            skLineSegment(sketch, "E368", {"start": v(708.12, -750.06) * mm, "end": v(706.6, -750.06) * mm});
            skLineSegment(sketch, "E369", {"start": v(706.6, -750.06) * mm, "end": v(704.53, -741.63) * mm});
            skLineSegment(sketch, "E370", {"start": v(704.53, -741.63) * mm, "end": v(702.5, -750.06) * mm});
            skLineSegment(sketch, "E371", {"start": v(702.5, -750.06) * mm, "end": v(701.02, -750.06) * mm});
            skLineSegment(sketch, "E372", {"start": v(701.02, -750.06) * mm, "end": v(698.42, -739.9) * mm});
            skLineSegment(sketch, "E373", {"start": v(698.42, -739.9) * mm, "end": v(699.8, -739.9) * mm});
            skLineSegment(sketch, "E374", {"start": v(699.8, -739.9) * mm, "end": v(701.85, -748.35) * mm});
            skLineSegment(sketch, "E375", {"start": v(701.85, -748.35) * mm, "end": v(703.89, -739.9) * mm});
            skLineSegment(sketch, "E376", {"start": v(703.89, -739.9) * mm, "end": v(705.26, -739.9) * mm});
            skLineSegment(sketch, "E377", {"start": v(705.26, -739.9) * mm, "end": v(707.31, -748.43) * mm});
            skLineSegment(sketch, "E378", {"start": v(707.31, -748.43) * mm, "end": v(709.34, -739.9) * mm});
            skLineSegment(sketch, "E379", {"start": v(709.34, -739.9) * mm, "end": v(710.67, -739.9) * mm});
            skLineSegment(sketch, "E380", {"start": v(732.96, -750.06) * mm, "end": v(731.44, -750.06) * mm});
            skLineSegment(sketch, "E381", {"start": v(731.44, -750.06) * mm, "end": v(726.95, -741.3) * mm});
            skLineSegment(sketch, "E382", {"start": v(726.95, -741.3) * mm, "end": v(726.95, -750.06) * mm});
            skLineSegment(sketch, "E383", {"start": v(726.95, -750.06) * mm, "end": v(725.7, -750.06) * mm});
            skLineSegment(sketch, "E384", {"start": v(725.7, -750.06) * mm, "end": v(725.7, -739.9) * mm});
            skLineSegment(sketch, "E385", {"start": v(725.7, -739.9) * mm, "end": v(727.6, -739.9) * mm});
            skLineSegment(sketch, "E386", {"start": v(727.6, -739.9) * mm, "end": v(731.7, -747.95) * mm});
            skLineSegment(sketch, "E387", {"start": v(731.7, -747.95) * mm, "end": v(731.7, -739.9) * mm});
            skLineSegment(sketch, "E388", {"start": v(731.7, -739.9) * mm, "end": v(732.96, -739.9) * mm});
            skLineSegment(sketch, "E389", {"start": v(732.96, -739.9) * mm, "end": v(732.96, -750.06) * mm});
            skLineSegment(sketch, "E390", {"start": v(731.04, -779.27) * mm, "end": v(728.25, -779.27) * mm});
            skLineSegment(sketch, "E391", {"start": v(728.25, -779.27) * mm, "end": v(723.8, -771.95) * mm});
            skLineSegment(sketch, "E392", {"start": v(723.8, -771.95) * mm, "end": v(719.26, -779.27) * mm});
            skLineSegment(sketch, "E393", {"start": v(719.26, -779.27) * mm, "end": v(716.63, -779.27) * mm});
            skLineSegment(sketch, "E394", {"start": v(716.63, -779.27) * mm, "end": v(722.44, -770.12) * mm});
            skLineSegment(sketch, "E395", {"start": v(722.44, -770.12) * mm, "end": v(716.8, -760.99) * mm});
            skLineSegment(sketch, "E396", {"start": v(716.8, -760.99) * mm, "end": v(719.58, -760.99) * mm});
            skLineSegment(sketch, "E397", {"start": v(719.58, -760.99) * mm, "end": v(723.95, -768.17) * mm});
            skLineSegment(sketch, "E398", {"start": v(723.95, -768.17) * mm, "end": v(728.38, -760.99) * mm});
            skLineSegment(sketch, "E399", {"start": v(728.38, -760.99) * mm, "end": v(731.02, -760.99) * mm});
            skLineSegment(sketch, "E400", {"start": v(731.02, -760.99) * mm, "end": v(725.3, -770) * mm});
            skLineSegment(sketch, "E401", {"start": v(725.3, -770) * mm, "end": v(731.04, -779.27) * mm});
            skLineSegment(sketch, "E402", {"start": v(745.77, -779.27) * mm, "end": v(742.98, -779.27) * mm});
            skLineSegment(sketch, "E403", {"start": v(742.98, -779.27) * mm, "end": v(738.52, -771.95) * mm});
            skLineSegment(sketch, "E404", {"start": v(738.52, -771.95) * mm, "end": v(734, -779.27) * mm});
            skLineSegment(sketch, "E405", {"start": v(734, -779.27) * mm, "end": v(731.36, -779.27) * mm});
            skLineSegment(sketch, "E406", {"start": v(731.36, -779.27) * mm, "end": v(737.17, -770.12) * mm});
            skLineSegment(sketch, "E407", {"start": v(737.17, -770.12) * mm, "end": v(731.54, -760.99) * mm});
            skLineSegment(sketch, "E408", {"start": v(731.54, -760.99) * mm, "end": v(734.31, -760.99) * mm});
            skLineSegment(sketch, "E409", {"start": v(734.31, -760.99) * mm, "end": v(738.68, -768.17) * mm});
            skLineSegment(sketch, "E410", {"start": v(738.68, -768.17) * mm, "end": v(743.11, -760.99) * mm});
            skLineSegment(sketch, "E411", {"start": v(743.11, -760.99) * mm, "end": v(745.75, -760.99) * mm});
            skLineSegment(sketch, "E412", {"start": v(745.75, -760.99) * mm, "end": v(740.03, -770) * mm});
            skLineSegment(sketch, "E413", {"start": v(740.03, -770) * mm, "end": v(745.77, -779.27) * mm});
            skLineSegment(sketch, "E414", {"start": v(758.2, -779.27) * mm, "end": v(747.6, -779.27) * mm});
            skLineSegment(sketch, "E415", {"start": v(747.6, -779.27) * mm, "end": v(747.6, -760.99) * mm});
            skLineSegment(sketch, "E416", {"start": v(747.6, -760.99) * mm, "end": v(750.03, -760.99) * mm});
            skLineSegment(sketch, "E417", {"start": v(750.03, -760.99) * mm, "end": v(750.03, -777.11) * mm});
            skLineSegment(sketch, "E418", {"start": v(750.03, -777.11) * mm, "end": v(758.2, -777.11) * mm});
            skLineSegment(sketch, "E419", {"start": v(758.2, -777.11) * mm, "end": v(758.2, -779.27) * mm});
            skLineSegment(sketch, "E420", {"start": v(780.55, -760.99) * mm, "end": v(775.96, -779.27) * mm});
            skLineSegment(sketch, "E421", {"start": v(775.96, -779.27) * mm, "end": v(773.22, -779.27) * mm});
            skLineSegment(sketch, "E422", {"start": v(773.22, -779.27) * mm, "end": v(769.5, -764.1) * mm});
            skLineSegment(sketch, "E423", {"start": v(769.5, -764.1) * mm, "end": v(765.86, -779.27) * mm});
            skLineSegment(sketch, "E424", {"start": v(765.86, -779.27) * mm, "end": v(763.19, -779.27) * mm});
            skLineSegment(sketch, "E425", {"start": v(763.19, -779.27) * mm, "end": v(758.5, -760.99) * mm});
            skLineSegment(sketch, "E426", {"start": v(758.5, -760.99) * mm, "end": v(761, -760.99) * mm});
            skLineSegment(sketch, "E427", {"start": v(761, -760.99) * mm, "end": v(764.69, -776.2) * mm});
            skLineSegment(sketch, "E428", {"start": v(764.69, -776.2) * mm, "end": v(768.34, -760.99) * mm});
            skLineSegment(sketch, "E429", {"start": v(768.34, -760.99) * mm, "end": v(770.81, -760.99) * mm});
            skLineSegment(sketch, "E430", {"start": v(770.81, -760.99) * mm, "end": v(774.5, -776.34) * mm});
            skLineSegment(sketch, "E431", {"start": v(774.5, -776.34) * mm, "end": v(778.17, -760.99) * mm});
            skLineSegment(sketch, "E432", {"start": v(778.17, -760.99) * mm, "end": v(780.55, -760.99) * mm});
            skLineSegment(sketch, "E433", {"start": v(809.7, -782.96) * mm, "end": v(795.58, -782.96) * mm});
            skLineSegment(sketch, "E434", {"start": v(795.58, -782.96) * mm, "end": v(795.58, -781.36) * mm});
            skLineSegment(sketch, "E435", {"start": v(795.58, -781.36) * mm, "end": v(809.7, -781.36) * mm});
            skLineSegment(sketch, "E436", {"start": v(809.7, -781.36) * mm, "end": v(809.7, -782.96) * mm});
            skLineSegment(sketch, "E437", {"start": v(855.44, -779.27) * mm, "end": v(853.13, -779.27) * mm});
            skLineSegment(sketch, "E438", {"start": v(853.13, -779.27) * mm, "end": v(853.13, -760.17) * mm});
            skLineSegment(sketch, "E439", {"start": v(853.13, -760.17) * mm, "end": v(855.44, -760.17) * mm});
            skLineSegment(sketch, "E440", {"start": v(855.44, -760.17) * mm, "end": v(855.44, -779.27) * mm});
            skLineSegment(sketch, "E441", {"start": v(861.18, -763.26) * mm, "end": v(858.56, -763.26) * mm});
            skLineSegment(sketch, "E442", {"start": v(858.56, -763.26) * mm, "end": v(858.56, -760.87) * mm});
            skLineSegment(sketch, "E443", {"start": v(858.56, -760.87) * mm, "end": v(861.18, -760.87) * mm});
            skLineSegment(sketch, "E444", {"start": v(861.18, -760.87) * mm, "end": v(861.18, -763.26) * mm});
            skLineSegment(sketch, "E445", {"start": v(861.02, -779.27) * mm, "end": v(858.72, -779.27) * mm});
            skLineSegment(sketch, "E446", {"start": v(858.72, -779.27) * mm, "end": v(858.72, -765.56) * mm});
            skLineSegment(sketch, "E447", {"start": v(858.72, -765.56) * mm, "end": v(861.02, -765.56) * mm});
            skLineSegment(sketch, "E448", {"start": v(861.02, -765.56) * mm, "end": v(861.02, -779.27) * mm});
            skLineSegment(sketch, "E449", {"start": v(539.85, -635) * mm, "end": v(539.85, -626.04) * mm});
            skLineSegment(sketch, "E450", {"start": v(539.85, -626.04) * mm, "end": v(536.44, -626.04) * mm});
            skLineSegment(sketch, "E451", {"start": v(536.44, -626.04) * mm, "end": v(536.44, -624.84) * mm});
            skLineSegment(sketch, "E452", {"start": v(536.44, -624.84) * mm, "end": v(544.61, -624.84) * mm});
            skLineSegment(sketch, "E453", {"start": v(544.61, -624.84) * mm, "end": v(544.61, -626.04) * mm});
            skLineSegment(sketch, "E454", {"start": v(544.61, -626.04) * mm, "end": v(541.2, -626.04) * mm});
            skLineSegment(sketch, "E455", {"start": v(541.2, -626.04) * mm, "end": v(541.2, -635) * mm});
            skLineSegment(sketch, "E456", {"start": v(541.2, -635) * mm, "end": v(539.85, -635) * mm});
            skLineSegment(sketch, "E457", {"start": v(549.15, -635) * mm, "end": v(545.21, -635) * mm});
            skLineSegment(sketch, "E458", {"start": v(545.21, -635) * mm, "end": v(545.21, -633.96) * mm});
            skLineSegment(sketch, "E459", {"start": v(545.21, -633.96) * mm, "end": v(546.5, -633.96) * mm});
            skLineSegment(sketch, "E460", {"start": v(546.5, -633.96) * mm, "end": v(546.5, -625.88) * mm});
            skLineSegment(sketch, "E461", {"start": v(546.5, -625.88) * mm, "end": v(545.21, -625.88) * mm});
            skLineSegment(sketch, "E462", {"start": v(545.21, -625.88) * mm, "end": v(545.21, -624.84) * mm});
            skLineSegment(sketch, "E463", {"start": v(545.21, -624.84) * mm, "end": v(549.15, -624.84) * mm});
            skLineSegment(sketch, "E464", {"start": v(549.15, -624.84) * mm, "end": v(549.15, -625.88) * mm});
            skLineSegment(sketch, "E465", {"start": v(549.15, -625.88) * mm, "end": v(547.86, -625.88) * mm});
            skLineSegment(sketch, "E466", {"start": v(547.86, -625.88) * mm, "end": v(547.86, -633.96) * mm});
            skLineSegment(sketch, "E467", {"start": v(547.86, -633.96) * mm, "end": v(549.15, -633.96) * mm});
            skLineSegment(sketch, "E468", {"start": v(549.15, -633.96) * mm, "end": v(549.15, -635) * mm});
            skLineSegment(sketch, "E469", {"start": v(553.31, -635) * mm, "end": v(553.31, -626.04) * mm});
            skLineSegment(sketch, "E470", {"start": v(553.31, -626.04) * mm, "end": v(549.9, -626.04) * mm});
            skLineSegment(sketch, "E471", {"start": v(549.9, -626.04) * mm, "end": v(549.9, -624.84) * mm});
            skLineSegment(sketch, "E472", {"start": v(549.9, -624.84) * mm, "end": v(558.08, -624.84) * mm});
            skLineSegment(sketch, "E473", {"start": v(558.08, -624.84) * mm, "end": v(558.08, -626.04) * mm});
            skLineSegment(sketch, "E474", {"start": v(558.08, -626.04) * mm, "end": v(554.66, -626.04) * mm});
            skLineSegment(sketch, "E475", {"start": v(554.66, -626.04) * mm, "end": v(554.66, -635) * mm});
            skLineSegment(sketch, "E476", {"start": v(554.66, -635) * mm, "end": v(553.31, -635) * mm});
            skLineSegment(sketch, "E477", {"start": v(564.95, -635) * mm, "end": v(559.07, -635) * mm});
            skLineSegment(sketch, "E478", {"start": v(559.07, -635) * mm, "end": v(559.07, -624.84) * mm});
            skLineSegment(sketch, "E479", {"start": v(559.07, -624.84) * mm, "end": v(560.42, -624.84) * mm});
            skLineSegment(sketch, "E480", {"start": v(560.42, -624.84) * mm, "end": v(560.42, -633.8) * mm});
            skLineSegment(sketch, "E481", {"start": v(560.42, -633.8) * mm, "end": v(564.95, -633.8) * mm});
            skLineSegment(sketch, "E482", {"start": v(564.95, -633.8) * mm, "end": v(564.95, -635) * mm});
            skLineSegment(sketch, "E483", {"start": v(565.93, -635) * mm, "end": v(565.93, -624.84) * mm});
            skLineSegment(sketch, "E484", {"start": v(565.93, -624.84) * mm, "end": v(572.28, -624.84) * mm});
            skLineSegment(sketch, "E485", {"start": v(572.28, -624.84) * mm, "end": v(572.28, -626.04) * mm});
            skLineSegment(sketch, "E486", {"start": v(572.28, -626.04) * mm, "end": v(567.28, -626.04) * mm});
            skLineSegment(sketch, "E487", {"start": v(567.28, -626.04) * mm, "end": v(567.28, -628.83) * mm});
            skLineSegment(sketch, "E488", {"start": v(567.28, -628.83) * mm, "end": v(571.94, -628.83) * mm});
            skLineSegment(sketch, "E489", {"start": v(571.94, -628.83) * mm, "end": v(571.94, -630.03) * mm});
            skLineSegment(sketch, "E490", {"start": v(571.94, -630.03) * mm, "end": v(567.28, -630.03) * mm});
            skLineSegment(sketch, "E491", {"start": v(567.28, -630.03) * mm, "end": v(567.28, -633.8) * mm});
            skLineSegment(sketch, "E492", {"start": v(567.28, -633.8) * mm, "end": v(572.28, -633.8) * mm});
            skLineSegment(sketch, "E493", {"start": v(572.28, -633.8) * mm, "end": v(572.28, -635) * mm});
            skLineSegment(sketch, "E494", {"start": v(572.28, -635) * mm, "end": v(565.93, -635) * mm});
            skLineSegment(sketch, "E495", {"start": v(556.77, -750.06) * mm, "end": v(552.83, -750.06) * mm});
            skLineSegment(sketch, "E496", {"start": v(552.83, -750.06) * mm, "end": v(552.83, -749.03) * mm});
            skLineSegment(sketch, "E497", {"start": v(552.83, -749.03) * mm, "end": v(554.13, -749.03) * mm});
            skLineSegment(sketch, "E498", {"start": v(554.13, -749.03) * mm, "end": v(554.13, -740.94) * mm});
            skLineSegment(sketch, "E499", {"start": v(554.13, -740.94) * mm, "end": v(552.83, -740.94) * mm});
            skLineSegment(sketch, "E500", {"start": v(552.83, -740.94) * mm, "end": v(552.83, -739.9) * mm});
            skLineSegment(sketch, "E501", {"start": v(552.83, -739.9) * mm, "end": v(556.77, -739.9) * mm});
            skLineSegment(sketch, "E502", {"start": v(556.77, -739.9) * mm, "end": v(556.77, -740.94) * mm});
            skLineSegment(sketch, "E503", {"start": v(556.77, -740.94) * mm, "end": v(555.48, -740.94) * mm});
            skLineSegment(sketch, "E504", {"start": v(555.48, -740.94) * mm, "end": v(555.48, -749.03) * mm});
            skLineSegment(sketch, "E505", {"start": v(555.48, -749.03) * mm, "end": v(556.77, -749.03) * mm});
            skLineSegment(sketch, "E506", {"start": v(556.77, -749.03) * mm, "end": v(556.77, -750.06) * mm});
            skLineSegment(sketch, "E507", {"start": v(565.03, -750.06) * mm, "end": v(557.94, -750.06) * mm});
            skLineSegment(sketch, "E508", {"start": v(557.94, -750.06) * mm, "end": v(557.94, -748.8) * mm});
            skLineSegment(sketch, "E509", {"start": v(557.94, -748.8) * mm, "end": v(563.38, -741.1) * mm});
            skLineSegment(sketch, "E510", {"start": v(563.38, -741.1) * mm, "end": v(558.18, -741.1) * mm});
            skLineSegment(sketch, "E511", {"start": v(558.18, -741.1) * mm, "end": v(558.18, -739.9) * mm});
            skLineSegment(sketch, "E512", {"start": v(558.18, -739.9) * mm, "end": v(564.9, -739.9) * mm});
            skLineSegment(sketch, "E513", {"start": v(564.9, -739.9) * mm, "end": v(564.9, -741.13) * mm});
            skLineSegment(sketch, "E514", {"start": v(564.9, -741.13) * mm, "end": v(559.4, -748.86) * mm});
            skLineSegment(sketch, "E515", {"start": v(559.4, -748.86) * mm, "end": v(565.03, -748.86) * mm});
            skLineSegment(sketch, "E516", {"start": v(565.03, -748.86) * mm, "end": v(565.03, -750.06) * mm});
            skLineSegment(sketch, "E517", {"start": v(566.43, -750.06) * mm, "end": v(566.43, -739.9) * mm});
            skLineSegment(sketch, "E518", {"start": v(566.43, -739.9) * mm, "end": v(572.78, -739.9) * mm});
            skLineSegment(sketch, "E519", {"start": v(572.78, -739.9) * mm, "end": v(572.78, -741.1) * mm});
            skLineSegment(sketch, "E520", {"start": v(572.78, -741.1) * mm, "end": v(567.78, -741.1) * mm});
            skLineSegment(sketch, "E521", {"start": v(567.78, -741.1) * mm, "end": v(567.78, -743.89) * mm});
            skLineSegment(sketch, "E522", {"start": v(567.78, -743.89) * mm, "end": v(572.44, -743.89) * mm});
            skLineSegment(sketch, "E523", {"start": v(572.44, -743.89) * mm, "end": v(572.44, -745.09) * mm});
            skLineSegment(sketch, "E524", {"start": v(572.44, -745.09) * mm, "end": v(567.78, -745.09) * mm});
            skLineSegment(sketch, "E525", {"start": v(567.78, -745.09) * mm, "end": v(567.78, -748.86) * mm});
            skLineSegment(sketch, "E526", {"start": v(567.78, -748.86) * mm, "end": v(572.78, -748.86) * mm});
            skLineSegment(sketch, "E527", {"start": v(572.78, -748.86) * mm, "end": v(572.78, -750.06) * mm});
            skLineSegment(sketch, "E528", {"start": v(572.78, -750.06) * mm, "end": v(566.43, -750.06) * mm});
            skLineSegment(sketch, "E529", {"start": v(552.64, -800.86) * mm, "end": v(556.06, -790.7) * mm});
            skLineSegment(sketch, "E530", {"start": v(556.06, -790.7) * mm, "end": v(557.72, -790.7) * mm});
            skLineSegment(sketch, "E531", {"start": v(557.72, -790.7) * mm, "end": v(561.15, -800.86) * mm});
            skLineSegment(sketch, "E532", {"start": v(561.15, -800.86) * mm, "end": v(559.72, -800.86) * mm});
            skLineSegment(sketch, "E533", {"start": v(559.72, -800.86) * mm, "end": v(558.8, -798.02) * mm});
            skLineSegment(sketch, "E534", {"start": v(558.8, -798.02) * mm, "end": v(554.92, -798.02) * mm});
            skLineSegment(sketch, "E535", {"start": v(554.92, -798.02) * mm, "end": v(554, -800.86) * mm});
            skLineSegment(sketch, "E536", {"start": v(554, -800.86) * mm, "end": v(552.64, -800.86) * mm});
            skLineSegment(sketch, "E537", {"start": v(558.43, -796.87) * mm, "end": v(556.86, -792.08) * mm});
            skLineSegment(sketch, "E538", {"start": v(556.86, -792.08) * mm, "end": v(555.3, -796.87) * mm});
            skLineSegment(sketch, "E539", {"start": v(555.3, -796.87) * mm, "end": v(558.43, -796.87) * mm});
            skLineSegment(sketch, "E540", {"start": v(568, -800.86) * mm, "end": v(562.12, -800.86) * mm});
            skLineSegment(sketch, "E541", {"start": v(562.12, -800.86) * mm, "end": v(562.12, -790.7) * mm});
            skLineSegment(sketch, "E542", {"start": v(562.12, -790.7) * mm, "end": v(563.47, -790.7) * mm});
            skLineSegment(sketch, "E543", {"start": v(563.47, -790.7) * mm, "end": v(563.47, -799.66) * mm});
            skLineSegment(sketch, "E544", {"start": v(563.47, -799.66) * mm, "end": v(568, -799.66) * mm});
            skLineSegment(sketch, "E545", {"start": v(568, -799.66) * mm, "end": v(568, -800.86) * mm});
            skLineSegment(sketch, "E546", {"start": v(568.97, -800.86) * mm, "end": v(568.97, -790.7) * mm});
            skLineSegment(sketch, "E547", {"start": v(568.97, -790.7) * mm, "end": v(575.33, -790.7) * mm});
            skLineSegment(sketch, "E548", {"start": v(575.33, -790.7) * mm, "end": v(575.33, -791.9) * mm});
            skLineSegment(sketch, "E549", {"start": v(575.33, -791.9) * mm, "end": v(570.33, -791.9) * mm});
            skLineSegment(sketch, "E550", {"start": v(570.33, -791.9) * mm, "end": v(570.33, -794.69) * mm});
            skLineSegment(sketch, "E551", {"start": v(570.33, -794.69) * mm, "end": v(574.98, -794.69) * mm});
            skLineSegment(sketch, "E552", {"start": v(574.98, -794.69) * mm, "end": v(574.98, -795.89) * mm});
            skLineSegment(sketch, "E553", {"start": v(574.98, -795.89) * mm, "end": v(570.33, -795.89) * mm});
            skLineSegment(sketch, "E554", {"start": v(570.33, -795.89) * mm, "end": v(570.33, -799.66) * mm});
            skLineSegment(sketch, "E555", {"start": v(570.33, -799.66) * mm, "end": v(575.33, -799.66) * mm});
            skLineSegment(sketch, "E556", {"start": v(575.33, -799.66) * mm, "end": v(575.33, -800.86) * mm});
            skLineSegment(sketch, "E557", {"start": v(575.33, -800.86) * mm, "end": v(568.97, -800.86) * mm});
            skLineSegment(sketch, "E558", {"start": v(1013.22, -749.8) * mm, "end": v(1013.22, -739.65) * mm});
            skLineSegment(sketch, "E559", {"start": v(1013.22, -739.65) * mm, "end": v(1019.57, -739.65) * mm});
            skLineSegment(sketch, "E560", {"start": v(1019.57, -739.65) * mm, "end": v(1019.57, -740.85) * mm});
            skLineSegment(sketch, "E561", {"start": v(1019.57, -740.85) * mm, "end": v(1014.57, -740.85) * mm});
            skLineSegment(sketch, "E562", {"start": v(1014.57, -740.85) * mm, "end": v(1014.57, -743.64) * mm});
            skLineSegment(sketch, "E563", {"start": v(1014.57, -743.64) * mm, "end": v(1019.23, -743.64) * mm});
            skLineSegment(sketch, "E564", {"start": v(1019.23, -743.64) * mm, "end": v(1019.23, -744.84) * mm});
            skLineSegment(sketch, "E565", {"start": v(1019.23, -744.84) * mm, "end": v(1014.57, -744.84) * mm});
            skLineSegment(sketch, "E566", {"start": v(1014.57, -744.84) * mm, "end": v(1014.57, -748.6) * mm});
            skLineSegment(sketch, "E567", {"start": v(1014.57, -748.6) * mm, "end": v(1019.57, -748.6) * mm});
            skLineSegment(sketch, "E568", {"start": v(1019.57, -748.6) * mm, "end": v(1019.57, -749.8) * mm});
            skLineSegment(sketch, "E569", {"start": v(1019.57, -749.8) * mm, "end": v(1013.22, -749.8) * mm});
            skLineSegment(sketch, "E570", {"start": v(1028.45, -739.65) * mm, "end": v(1024.96, -749.8) * mm});
            skLineSegment(sketch, "E571", {"start": v(1024.96, -749.8) * mm, "end": v(1023.5, -749.8) * mm});
            skLineSegment(sketch, "E572", {"start": v(1023.5, -749.8) * mm, "end": v(1020, -739.65) * mm});
            skLineSegment(sketch, "E573", {"start": v(1020, -739.65) * mm, "end": v(1021.46, -739.65) * mm});
            skLineSegment(sketch, "E574", {"start": v(1021.46, -739.65) * mm, "end": v(1024.27, -748.08) * mm});
            skLineSegment(sketch, "E575", {"start": v(1024.27, -748.08) * mm, "end": v(1027.08, -739.65) * mm});
            skLineSegment(sketch, "E576", {"start": v(1027.08, -739.65) * mm, "end": v(1028.45, -739.65) * mm});
            skLineSegment(sketch, "E577", {"start": v(738.08, 388.87) * mm, "end": v(736.12, 388.87) * mm});
            skLineSegment(sketch, "E578", {"start": v(736.12, 388.87) * mm, "end": v(736.12, 391.2) * mm});
            skLineSegment(sketch, "E579", {"start": v(736.12, 391.2) * mm, "end": v(738.08, 391.2) * mm});
            skLineSegment(sketch, "E580", {"start": v(738.08, 391.2) * mm, "end": v(738.08, 388.87) * mm});
            skLineSegment(sketch, "E581", {"start": v(758.2, 394.97) * mm, "end": v(768.1, 394.97) * mm});
            skLineSegment(sketch, "E582", {"start": v(758.2, 392.94) * mm, "end": v(768.1, 394.97) * mm});
            skLineSegment(sketch, "E583", {"start": v(768.1, 394.97) * mm, "end": v(758.2, 397) * mm});
            skLineSegment(sketch, "E584", {"start": v(758.2, 397) * mm, "end": v(758.2, 392.94) * mm});
            skLineSegment(sketch, "E585", {"start": v(797.3, 394.97) * mm, "end": v(787.15, 394.97) * mm});
            skLineSegment(sketch, "E586", {"start": v(797.3, 397) * mm, "end": v(787.15, 394.97) * mm});
            skLineSegment(sketch, "E587", {"start": v(787.15, 394.97) * mm, "end": v(797.3, 392.94) * mm});
            skLineSegment(sketch, "E588", {"start": v(797.3, 392.94) * mm, "end": v(797.3, 397) * mm});
            skLineSegment(sketch, "E589", {"start": v(797.3, 394.97) * mm, "end": v(807.21, 394.97) * mm});
            skLineSegment(sketch, "E590", {"start": v(787.15, 296.93) * mm, "end": v(787.15, 407.67) * mm});
            skLineSegment(sketch, "E591", {"start": v(768.1, 296.93) * mm, "end": v(768.1, 407.67) * mm});
            skLineSegment(sketch, "E592", {"start": v(720.55, 303.02) * mm, "end": v(718.6, 303.02) * mm});
            skLineSegment(sketch, "E593", {"start": v(718.6, 303.02) * mm, "end": v(718.6, 305.36) * mm});
            skLineSegment(sketch, "E594", {"start": v(718.6, 305.36) * mm, "end": v(720.55, 305.36) * mm});
            skLineSegment(sketch, "E595", {"start": v(720.55, 305.36) * mm, "end": v(720.55, 303.02) * mm});
            skLineSegment(sketch, "E596", {"start": v(758.2, 309.12) * mm, "end": v(768.1, 309.12) * mm});
            skLineSegment(sketch, "E597", {"start": v(758.2, 307.09) * mm, "end": v(768.1, 309.12) * mm});
            skLineSegment(sketch, "E598", {"start": v(768.1, 309.12) * mm, "end": v(758.2, 311.15) * mm});
            skLineSegment(sketch, "E599", {"start": v(758.2, 311.15) * mm, "end": v(758.2, 307.09) * mm});
            skLineSegment(sketch, "E600", {"start": v(784.6, 309.12) * mm, "end": v(774.45, 309.12) * mm});
            skLineSegment(sketch, "E601", {"start": v(784.6, 311.15) * mm, "end": v(774.45, 309.12) * mm});
            skLineSegment(sketch, "E602", {"start": v(774.45, 309.12) * mm, "end": v(784.6, 307.09) * mm});
            skLineSegment(sketch, "E603", {"start": v(784.6, 307.09) * mm, "end": v(784.6, 311.15) * mm});
            skLineSegment(sketch, "E604", {"start": v(758.2, 309.12) * mm, "end": v(748.28, 309.12) * mm});
            skLineSegment(sketch, "E605", {"start": v(784.6, 309.12) * mm, "end": v(794.51, 309.12) * mm});
            skLineSegment(sketch, "E606", {"start": v(768.1, 296.93) * mm, "end": v(768.1, 321.82) * mm});
            skLineSegment(sketch, "E607", {"start": v(774.45, 281.18) * mm, "end": v(774.45, 321.82) * mm});
            skLineSegment(sketch, "E608", {"start": v(743.71, 309.12) * mm, "end": v(748.28, 309.12) * mm});
            skLineSegment(sketch, "E609", {"start": v(-44.5, 372.62) * mm, "end": v(-46.45, 372.62) * mm});
            skLineSegment(sketch, "E610", {"start": v(-46.45, 372.62) * mm, "end": v(-46.45, 374.95) * mm});
            skLineSegment(sketch, "E611", {"start": v(-46.45, 374.95) * mm, "end": v(-44.5, 374.95) * mm});
            skLineSegment(sketch, "E612", {"start": v(-44.5, 374.95) * mm, "end": v(-44.5, 372.62) * mm});
            skLineSegment(sketch, "E613", {"start": v(-578.1, 378.71) * mm, "end": v(-588.01, 378.71) * mm});
            skLineSegment(sketch, "E614", {"start": v(-578.1, 380.5) * mm, "end": v(-588.01, 378.71) * mm});
            skLineSegment(sketch, "E615", {"start": v(-588.01, 378.71) * mm, "end": v(-578.1, 376.68) * mm});
            skLineSegment(sketch, "E616", {"start": v(-578.1, 376.68) * mm, "end": v(-578.1, 380.5) * mm});
            skLineSegment(sketch, "E617", {"start": v(468.88, 378.71) * mm, "end": v(478.8, 378.71) * mm});
            skLineSegment(sketch, "E618", {"start": v(468.88, 376.68) * mm, "end": v(478.8, 378.71) * mm});
            skLineSegment(sketch, "E619", {"start": v(478.8, 378.71) * mm, "end": v(468.88, 380.5) * mm});
            skLineSegment(sketch, "E620", {"start": v(468.88, 380.5) * mm, "end": v(468.88, 376.68) * mm});
            skLineSegment(sketch, "E621", {"start": v(-578.1, 378.71) * mm, "end": v(-87.88, 378.71) * mm});
            skLineSegment(sketch, "E622", {"start": v(-21.34, 378.71) * mm, "end": v(468.88, 378.71) * mm});
            skLineSegment(sketch, "E623", {"start": v(-588.01, 296.93) * mm, "end": v(-588.01, 391.41) * mm});
            skLineSegment(sketch, "E624", {"start": v(478.8, 300.48) * mm, "end": v(478.8, 391.41) * mm});
            skLineSegment(sketch, "E625", {"start": v(-762.76, 48.47) * mm, "end": v(-762.76, 46.51) * mm});
            skLineSegment(sketch, "E626", {"start": v(-762.76, 46.51) * mm, "end": v(-765.1, 46.51) * mm});
            skLineSegment(sketch, "E627", {"start": v(-765.1, 46.51) * mm, "end": v(-765.1, 48.47) * mm});
            skLineSegment(sketch, "E628", {"start": v(-765.1, 48.47) * mm, "end": v(-762.76, 48.47) * mm});
            skLineSegment(sketch, "E629", {"start": v(-768.86, 283.72) * mm, "end": v(-768.86, 293.88) * mm});
            skLineSegment(sketch, "E630", {"start": v(-766.83, 283.72) * mm, "end": v(-768.86, 293.88) * mm});
            skLineSegment(sketch, "E631", {"start": v(-768.86, 293.88) * mm, "end": v(-770.9, 283.72) * mm});
            skLineSegment(sketch, "E632", {"start": v(-770.9, 283.72) * mm, "end": v(-766.83, 283.72) * mm});
            skLineSegment(sketch, "E633", {"start": v(-768.86, -197.87) * mm, "end": v(-768.86, -207.77) * mm});
            skLineSegment(sketch, "E634", {"start": v(-770.9, -197.87) * mm, "end": v(-768.86, -207.77) * mm});
            skLineSegment(sketch, "E635", {"start": v(-768.86, -207.77) * mm, "end": v(-766.83, -197.87) * mm});
            skLineSegment(sketch, "E636", {"start": v(-766.83, -197.87) * mm, "end": v(-770.9, -197.87) * mm});
            skLineSegment(sketch, "E637", {"start": v(-768.86, 283.72) * mm, "end": v(-768.86, 71.63) * mm});
            skLineSegment(sketch, "E638", {"start": v(-768.86, 14.22) * mm, "end": v(-768.86, -197.87) * mm});
            skLineSegment(sketch, "E639", {"start": v(-597.66, -207.77) * mm, "end": v(-618.49, -207.77) * mm});
            skLineSegment(sketch, "E640", {"start": v(-648.2, -207.77) * mm, "end": v(-781.56, -207.77) * mm});
            skLineSegment(sketch, "E641", {"start": v(-591.31, 293.88) * mm, "end": v(-618.49, 293.88) * mm});
            skLineSegment(sketch, "E642", {"start": v(-675.64, 293.88) * mm, "end": v(-781.56, 293.88) * mm});
            skLineSegment(sketch, "E643", {"start": v(-578.1, -207.77) * mm, "end": v(-578.87, -203.96) * mm});
            skLineSegment(sketch, "E644", {"start": v(-578.87, -203.96) * mm, "end": v(-580.9, -200.91) * mm});
            skLineSegment(sketch, "E645", {"start": v(-580.9, -200.91) * mm, "end": v(-578.1, -207.77) * mm});
            skLineSegment(sketch, "E646", {"start": v(-578.1, -207.77) * mm, "end": v(-580.9, -200.91) * mm});
            skLineSegment(sketch, "E647", {"start": v(-580.9, -200.91) * mm, "end": v(-584.2, -198.63) * mm});
            skLineSegment(sketch, "E648", {"start": v(-584.2, -198.63) * mm, "end": v(-578.1, -207.77) * mm});
            skLineSegment(sketch, "E649", {"start": v(-578.1, -207.77) * mm, "end": v(-584.2, -198.63) * mm});
            skLineSegment(sketch, "E650", {"start": v(-584.2, -198.63) * mm, "end": v(-588.01, -197.87) * mm});
            skLineSegment(sketch, "E651", {"start": v(-588.01, -197.87) * mm, "end": v(-578.1, -207.77) * mm});
            skLineSegment(sketch, "E652", {"start": v(-597.92, -207.77) * mm, "end": v(-597.15, -211.84) * mm});
            skLineSegment(sketch, "E653", {"start": v(-597.15, -211.84) * mm, "end": v(-595.12, -214.88) * mm});
            skLineSegment(sketch, "E654", {"start": v(-595.12, -214.88) * mm, "end": v(-597.92, -207.77) * mm});
            skLineSegment(sketch, "E655", {"start": v(-597.92, -207.77) * mm, "end": v(-595.12, -214.88) * mm});
            skLineSegment(sketch, "E656", {"start": v(-595.12, -214.88) * mm, "end": v(-591.82, -217.17) * mm});
            skLineSegment(sketch, "E657", {"start": v(-591.82, -217.17) * mm, "end": v(-597.92, -207.77) * mm});
            skLineSegment(sketch, "E658", {"start": v(-597.92, -207.77) * mm, "end": v(-591.82, -217.17) * mm});
            skLineSegment(sketch, "E659", {"start": v(-591.82, -217.17) * mm, "end": v(-588.01, -217.93) * mm});
            skLineSegment(sketch, "E660", {"start": v(-588.01, -217.93) * mm, "end": v(-597.92, -207.77) * mm});
            skLineSegment(sketch, "E661", {"start": v(-588.01, -207.77) * mm, "end": v(-578.1, -207.77) * mm});
            skLineSegment(sketch, "E662", {"start": v(-578.1, -207.77) * mm, "end": v(-588.01, -197.87) * mm});
            skLineSegment(sketch, "E663", {"start": v(-588.01, -197.87) * mm, "end": v(-588.01, -207.77) * mm});
            skLineSegment(sketch, "E664", {"start": v(-588.01, -207.77) * mm, "end": v(-588.01, -197.87) * mm});
            skLineSegment(sketch, "E665", {"start": v(-588.01, -197.87) * mm, "end": v(-588.01, -217.93) * mm});
            skLineSegment(sketch, "E666", {"start": v(-588.01, -217.93) * mm, "end": v(-588.01, -207.77) * mm});
            skLineSegment(sketch, "E667", {"start": v(-588.01, -207.77) * mm, "end": v(-588.01, -217.93) * mm});
            skLineSegment(sketch, "E668", {"start": v(-597.92, -207.77) * mm, "end": v(-588.01, -207.77) * mm});
            skLineSegment(sketch, "E669", {"start": v(-581.92, -310.68) * mm, "end": v(-581.91, -312.64) * mm});
            skLineSegment(sketch, "E670", {"start": v(-581.91, -312.64) * mm, "end": v(-584.25, -312.64) * mm});
            skLineSegment(sketch, "E671", {"start": v(-584.25, -312.64) * mm, "end": v(-584.25, -310.69) * mm});
            skLineSegment(sketch, "E672", {"start": v(-584.25, -310.69) * mm, "end": v(-581.92, -310.68) * mm});
            skLineSegment(sketch, "E673", {"start": v(-588.01, -219.96) * mm, "end": v(-588.01, -233.43) * mm});
            skLineSegment(sketch, "E674", {"start": v(-588.01, -233.43) * mm, "end": v(-588.01, -262.13) * mm});
            skLineSegment(sketch, "E675", {"start": v(-588.01, -262.13) * mm, "end": v(-588.01, -287.78) * mm});
            skLineSegment(sketch, "E676", {"start": v(-556.52, -310.69) * mm, "end": v(-556.51, -312.64) * mm});
            skLineSegment(sketch, "E677", {"start": v(-556.51, -312.64) * mm, "end": v(-558.85, -312.64) * mm});
            skLineSegment(sketch, "E678", {"start": v(-558.85, -312.64) * mm, "end": v(-558.85, -310.69) * mm});
            skLineSegment(sketch, "E679", {"start": v(-558.85, -310.69) * mm, "end": v(-556.52, -310.69) * mm});
            skLineSegment(sketch, "E680", {"start": v(-560.71, -300.39) * mm, "end": v(-560.7, -301.83) * mm});
            skLineSegment(sketch, "E681", {"start": v(-560.7, -301.83) * mm, "end": v(-556.52, -301.83) * mm});
            skLineSegment(sketch, "E682", {"start": v(-556.52, -301.83) * mm, "end": v(-556.52, -303.4) * mm});
            skLineSegment(sketch, "E683", {"start": v(-556.52, -303.4) * mm, "end": v(-560.7, -303.4) * mm});
            skLineSegment(sketch, "E684", {"start": v(-560.7, -303.4) * mm, "end": v(-560.7, -308.8) * mm});
            skLineSegment(sketch, "E685", {"start": v(-560.7, -308.8) * mm, "end": v(-562.42, -308.8) * mm});
            skLineSegment(sketch, "E686", {"start": v(-562.42, -308.8) * mm, "end": v(-568.7, -303.35) * mm});
            skLineSegment(sketch, "E687", {"start": v(-568.7, -303.35) * mm, "end": v(-568.7, -301.84) * mm});
            skLineSegment(sketch, "E688", {"start": v(-568.7, -301.84) * mm, "end": v(-562.02, -301.84) * mm});
            skLineSegment(sketch, "E689", {"start": v(-562.02, -301.84) * mm, "end": v(-562.02, -300.39) * mm});
            skLineSegment(sketch, "E690", {"start": v(-562.02, -300.39) * mm, "end": v(-560.71, -300.39) * mm});
            skLineSegment(sketch, "E691", {"start": v(-562.02, -303.4) * mm, "end": v(-566.78, -303.41) * mm});
            skLineSegment(sketch, "E692", {"start": v(-566.78, -303.41) * mm, "end": v(-562.02, -307.52) * mm});
            skLineSegment(sketch, "E693", {"start": v(-562.02, -307.52) * mm, "end": v(-562.02, -303.4) * mm});
            skLineSegment(sketch, "E694", {"start": v(-562.61, -199.39) * mm, "end": v(-562.61, -225.55) * mm});
            skLineSegment(sketch, "E695", {"start": v(-562.61, -225.55) * mm, "end": v(-562.61, -258.32) * mm});
            skLineSegment(sketch, "E696", {"start": v(-562.61, -258.32) * mm, "end": v(-562.61, -287.78) * mm});
            skLineSegment(sketch, "E697", {"start": v(-516.08, -323.95) * mm, "end": v(-505.72, -329.21) * mm});
            skLineSegment(sketch, "E698", {"start": v(-505.72, -329.21) * mm, "end": v(-505.71, -330.96) * mm});
            skLineSegment(sketch, "E699", {"start": v(-505.71, -330.96) * mm, "end": v(-516.47, -325.38) * mm});
            skLineSegment(sketch, "E700", {"start": v(-516.47, -325.38) * mm, "end": v(-516.47, -331.68) * mm});
            skLineSegment(sketch, "E701", {"start": v(-516.47, -331.68) * mm, "end": v(-517.9, -331.68) * mm});
            skLineSegment(sketch, "E702", {"start": v(-517.9, -331.68) * mm, "end": v(-517.9, -323.95) * mm});
            skLineSegment(sketch, "E703", {"start": v(-517.9, -323.95) * mm, "end": v(-516.08, -323.95) * mm});
            skLineSegment(sketch, "E704", {"start": v(-505.72, -310.69) * mm, "end": v(-505.71, -312.64) * mm});
            skLineSegment(sketch, "E705", {"start": v(-505.71, -312.64) * mm, "end": v(-508.05, -312.64) * mm});
            skLineSegment(sketch, "E706", {"start": v(-508.05, -312.64) * mm, "end": v(-508.05, -310.69) * mm});
            skLineSegment(sketch, "E707", {"start": v(-508.05, -310.69) * mm, "end": v(-505.72, -310.69) * mm});
            skLineSegment(sketch, "E708", {"start": v(-511.81, 261.87) * mm, "end": v(-511.81, 82.04) * mm});
            skLineSegment(sketch, "E709", {"start": v(-511.81, -104.4) * mm, "end": v(-511.81, -287.78) * mm});
            skLineSegment(sketch, "E710", {"start": v(-511.81, 82.04) * mm, "end": v(-511.81, 43.43) * mm});
            skLineSegment(sketch, "E711", {"start": v(-511.81, 42.42) * mm, "end": v(-511.81, -104.4) * mm});
            skLineSegment(sketch, "E712", {"start": v(-465.28, -314.8) * mm, "end": v(-454.92, -320.07) * mm});
            skLineSegment(sketch, "E713", {"start": v(-454.92, -320.07) * mm, "end": v(-454.92, -321.81) * mm});
            skLineSegment(sketch, "E714", {"start": v(-454.92, -321.81) * mm, "end": v(-465.67, -316.23) * mm});
            skLineSegment(sketch, "E715", {"start": v(-465.67, -316.23) * mm, "end": v(-465.67, -322.54) * mm});
            skLineSegment(sketch, "E716", {"start": v(-465.67, -322.54) * mm, "end": v(-467.1, -322.54) * mm});
            skLineSegment(sketch, "E717", {"start": v(-467.1, -322.54) * mm, "end": v(-467.1, -314.8) * mm});
            skLineSegment(sketch, "E718", {"start": v(-467.1, -314.8) * mm, "end": v(-465.28, -314.8) * mm});
            skLineSegment(sketch, "E719", {"start": v(-454.92, -310.69) * mm, "end": v(-454.91, -312.64) * mm});
            skLineSegment(sketch, "E720", {"start": v(-454.91, -312.64) * mm, "end": v(-457.25, -312.64) * mm});
            skLineSegment(sketch, "E721", {"start": v(-457.25, -312.64) * mm, "end": v(-457.25, -310.69) * mm});
            skLineSegment(sketch, "E722", {"start": v(-457.25, -310.69) * mm, "end": v(-454.92, -310.69) * mm});
            skLineSegment(sketch, "E723", {"start": v(-461.01, -199.39) * mm, "end": v(-461.01, -225.55) * mm});
            skLineSegment(sketch, "E724", {"start": v(-461.01, -225.55) * mm, "end": v(-461.01, -258.32) * mm});
            skLineSegment(sketch, "E725", {"start": v(-461.01, -258.32) * mm, "end": v(-461.01, -287.78) * mm});
            skLineSegment(sketch, "E726", {"start": v(-103.51, -332.9) * mm, "end": v(-103.5, -334.35) * mm});
            skLineSegment(sketch, "E727", {"start": v(-103.5, -334.35) * mm, "end": v(-99.32, -334.35) * mm});
            skLineSegment(sketch, "E728", {"start": v(-99.32, -334.35) * mm, "end": v(-99.32, -335.92) * mm});
            skLineSegment(sketch, "E729", {"start": v(-99.32, -335.92) * mm, "end": v(-103.5, -335.92) * mm});
            skLineSegment(sketch, "E730", {"start": v(-103.5, -335.92) * mm, "end": v(-103.5, -341.3) * mm});
            skLineSegment(sketch, "E731", {"start": v(-103.5, -341.3) * mm, "end": v(-105.22, -341.3) * mm});
            skLineSegment(sketch, "E732", {"start": v(-105.22, -341.3) * mm, "end": v(-111.5, -335.86) * mm});
            skLineSegment(sketch, "E733", {"start": v(-111.5, -335.86) * mm, "end": v(-111.5, -334.35) * mm});
            skLineSegment(sketch, "E734", {"start": v(-111.5, -334.35) * mm, "end": v(-104.82, -334.35) * mm});
            skLineSegment(sketch, "E735", {"start": v(-104.82, -334.35) * mm, "end": v(-104.82, -332.9) * mm});
            skLineSegment(sketch, "E736", {"start": v(-104.82, -332.9) * mm, "end": v(-103.51, -332.9) * mm});
            skLineSegment(sketch, "E737", {"start": v(-104.82, -335.92) * mm, "end": v(-109.58, -335.92) * mm});
            skLineSegment(sketch, "E738", {"start": v(-109.58, -335.92) * mm, "end": v(-104.82, -340.03) * mm});
            skLineSegment(sketch, "E739", {"start": v(-104.82, -340.03) * mm, "end": v(-104.82, -335.92) * mm});
            skLineSegment(sketch, "E740", {"start": v(-99.32, -310.69) * mm, "end": v(-99.31, -312.64) * mm});
            skLineSegment(sketch, "E741", {"start": v(-99.31, -312.64) * mm, "end": v(-101.65, -312.65) * mm});
            skLineSegment(sketch, "E742", {"start": v(-101.65, -312.65) * mm, "end": v(-101.65, -310.69) * mm});
            skLineSegment(sketch, "E743", {"start": v(-101.65, -310.69) * mm, "end": v(-99.32, -310.69) * mm});
            skLineSegment(sketch, "E744", {"start": v(-105.41, -199.39) * mm, "end": v(-105.41, -225.55) * mm});
            skLineSegment(sketch, "E745", {"start": v(-105.41, -225.55) * mm, "end": v(-105.41, -258.32) * mm});
            skLineSegment(sketch, "E746", {"start": v(-105.41, -258.32) * mm, "end": v(-105.41, -287.78) * mm});
            skLineSegment(sketch, "E747", {"start": v(-48.52, -310.69) * mm, "end": v(-48.51, -312.64) * mm});
            skLineSegment(sketch, "E748", {"start": v(-48.51, -312.64) * mm, "end": v(-50.85, -312.64) * mm});
            skLineSegment(sketch, "E749", {"start": v(-50.85, -312.64) * mm, "end": v(-50.85, -310.69) * mm});
            skLineSegment(sketch, "E750", {"start": v(-50.85, -310.69) * mm, "end": v(-48.52, -310.69) * mm});
            skLineSegment(sketch, "E751", {"start": v(-52.71, -300.38) * mm, "end": v(-52.7, -301.83) * mm});
            skLineSegment(sketch, "E752", {"start": v(-52.7, -301.83) * mm, "end": v(-48.52, -301.83) * mm});
            skLineSegment(sketch, "E753", {"start": v(-48.52, -301.83) * mm, "end": v(-48.52, -303.4) * mm});
            skLineSegment(sketch, "E754", {"start": v(-48.52, -303.4) * mm, "end": v(-52.7, -303.4) * mm});
            skLineSegment(sketch, "E755", {"start": v(-52.7, -303.4) * mm, "end": v(-52.7, -308.8) * mm});
            skLineSegment(sketch, "E756", {"start": v(-52.7, -308.8) * mm, "end": v(-54.42, -308.8) * mm});
            skLineSegment(sketch, "E757", {"start": v(-54.42, -308.8) * mm, "end": v(-60.7, -303.34) * mm});
            skLineSegment(sketch, "E758", {"start": v(-60.7, -303.34) * mm, "end": v(-60.7, -301.84) * mm});
            skLineSegment(sketch, "E759", {"start": v(-60.7, -301.84) * mm, "end": v(-54.02, -301.83) * mm});
            skLineSegment(sketch, "E760", {"start": v(-54.02, -301.83) * mm, "end": v(-54.02, -300.39) * mm});
            skLineSegment(sketch, "E761", {"start": v(-54.02, -300.39) * mm, "end": v(-52.71, -300.38) * mm});
            skLineSegment(sketch, "E762", {"start": v(-54.02, -303.4) * mm, "end": v(-58.78, -303.4) * mm});
            skLineSegment(sketch, "E763", {"start": v(-58.78, -303.4) * mm, "end": v(-54.02, -307.52) * mm});
            skLineSegment(sketch, "E764", {"start": v(-54.02, -307.52) * mm, "end": v(-54.02, -303.4) * mm});
            skLineSegment(sketch, "E765", {"start": v(-54.61, -217.42) * mm, "end": v(-54.61, -287.78) * mm});
            skLineSegment(sketch, "E766", {"start": v(-1.91, -314.6) * mm, "end": v(-1.9, -316.06) * mm});
            skLineSegment(sketch, "E767", {"start": v(-1.9, -316.06) * mm, "end": v(2.28, -316.06) * mm});
            skLineSegment(sketch, "E768", {"start": v(2.28, -316.06) * mm, "end": v(2.28, -317.63) * mm});
            skLineSegment(sketch, "E769", {"start": v(2.28, -317.63) * mm, "end": v(-1.9, -317.63) * mm});
            skLineSegment(sketch, "E770", {"start": v(-1.9, -317.63) * mm, "end": v(-1.9, -323.02) * mm});
            skLineSegment(sketch, "E771", {"start": v(-1.9, -323.02) * mm, "end": v(-3.62, -323.02) * mm});
            skLineSegment(sketch, "E772", {"start": v(-3.62, -323.02) * mm, "end": v(-9.9, -317.57) * mm});
            skLineSegment(sketch, "E773", {"start": v(-9.9, -317.57) * mm, "end": v(-9.9, -316.06) * mm});
            skLineSegment(sketch, "E774", {"start": v(-9.9, -316.06) * mm, "end": v(-3.22, -316.06) * mm});
            skLineSegment(sketch, "E775", {"start": v(-3.22, -316.06) * mm, "end": v(-3.22, -314.61) * mm});
            skLineSegment(sketch, "E776", {"start": v(-3.22, -314.61) * mm, "end": v(-1.91, -314.6) * mm});
            skLineSegment(sketch, "E777", {"start": v(-3.22, -317.63) * mm, "end": v(-7.98, -317.63) * mm});
            skLineSegment(sketch, "E778", {"start": v(-7.98, -317.63) * mm, "end": v(-3.22, -321.74) * mm});
            skLineSegment(sketch, "E779", {"start": v(-3.22, -321.74) * mm, "end": v(-3.22, -317.63) * mm});
            skLineSegment(sketch, "E780", {"start": v(2.28, -310.69) * mm, "end": v(2.29, -312.64) * mm});
            skLineSegment(sketch, "E781", {"start": v(2.29, -312.64) * mm, "end": v(-0.05, -312.64) * mm});
            skLineSegment(sketch, "E782", {"start": v(-0.05, -312.64) * mm, "end": v(-0.05, -310.69) * mm});
            skLineSegment(sketch, "E783", {"start": v(-0.05, -310.69) * mm, "end": v(2.28, -310.69) * mm});
            skLineSegment(sketch, "E784", {"start": v(-3.81, -199.39) * mm, "end": v(-3.81, -225.55) * mm});
            skLineSegment(sketch, "E785", {"start": v(-3.81, -225.55) * mm, "end": v(-3.81, -258.32) * mm});
            skLineSegment(sketch, "E786", {"start": v(-3.81, -258.32) * mm, "end": v(-3.81, -287.78) * mm});
            skLineSegment(sketch, "E787", {"start": v(357.88, -310.69) * mm, "end": v(357.89, -312.64) * mm});
            skLineSegment(sketch, "E788", {"start": v(357.89, -312.64) * mm, "end": v(355.55, -312.64) * mm});
            skLineSegment(sketch, "E789", {"start": v(355.55, -312.64) * mm, "end": v(355.55, -310.69) * mm});
            skLineSegment(sketch, "E790", {"start": v(355.55, -310.69) * mm, "end": v(357.88, -310.69) * mm});
            skLineSegment(sketch, "E791", {"start": v(351.8, -199.39) * mm, "end": v(351.8, -225.55) * mm});
            skLineSegment(sketch, "E792", {"start": v(351.8, -225.55) * mm, "end": v(351.8, -258.32) * mm});
            skLineSegment(sketch, "E793", {"start": v(351.8, -258.32) * mm, "end": v(351.8, -287.78) * mm});
            skLineSegment(sketch, "E794", {"start": v(408.68, -310.69) * mm, "end": v(408.69, -312.64) * mm});
            skLineSegment(sketch, "E795", {"start": v(408.69, -312.64) * mm, "end": v(406.35, -312.65) * mm});
            skLineSegment(sketch, "E796", {"start": v(406.35, -312.65) * mm, "end": v(406.35, -310.69) * mm});
            skLineSegment(sketch, "E797", {"start": v(406.35, -310.69) * mm, "end": v(408.68, -310.69) * mm});
            skLineSegment(sketch, "E798", {"start": v(402.6, 261.87) * mm, "end": v(402.6, 82.04) * mm});
            skLineSegment(sketch, "E799", {"start": v(402.6, -104.4) * mm, "end": v(402.6, -287.78) * mm});
            skLineSegment(sketch, "E800", {"start": v(402.6, 82.04) * mm, "end": v(402.6, 43.43) * mm});
            skLineSegment(sketch, "E801", {"start": v(402.6, 42.42) * mm, "end": v(402.6, -104.4) * mm});
            skLineSegment(sketch, "E802", {"start": v(455.29, -323.75) * mm, "end": v(455.3, -325.2) * mm});
            skLineSegment(sketch, "E803", {"start": v(455.3, -325.2) * mm, "end": v(459.48, -325.2) * mm});
            skLineSegment(sketch, "E804", {"start": v(459.48, -325.2) * mm, "end": v(459.48, -326.77) * mm});
            skLineSegment(sketch, "E805", {"start": v(459.48, -326.77) * mm, "end": v(455.3, -326.77) * mm});
            skLineSegment(sketch, "E806", {"start": v(455.3, -326.77) * mm, "end": v(455.3, -332.16) * mm});
            skLineSegment(sketch, "E807", {"start": v(455.3, -332.16) * mm, "end": v(453.58, -332.16) * mm});
            skLineSegment(sketch, "E808", {"start": v(453.58, -332.16) * mm, "end": v(447.3, -326.71) * mm});
            skLineSegment(sketch, "E809", {"start": v(447.3, -326.71) * mm, "end": v(447.3, -325.2) * mm});
            skLineSegment(sketch, "E810", {"start": v(447.3, -325.2) * mm, "end": v(453.98, -325.2) * mm});
            skLineSegment(sketch, "E811", {"start": v(453.98, -325.2) * mm, "end": v(453.98, -323.75) * mm});
            skLineSegment(sketch, "E812", {"start": v(453.98, -323.75) * mm, "end": v(455.29, -323.75) * mm});
            skLineSegment(sketch, "E813", {"start": v(453.98, -326.78) * mm, "end": v(449.22, -326.78) * mm});
            skLineSegment(sketch, "E814", {"start": v(449.22, -326.78) * mm, "end": v(453.98, -330.88) * mm});
            skLineSegment(sketch, "E815", {"start": v(453.98, -330.88) * mm, "end": v(453.98, -326.78) * mm});
            skLineSegment(sketch, "E816", {"start": v(459.48, -310.69) * mm, "end": v(459.49, -312.64) * mm});
            skLineSegment(sketch, "E817", {"start": v(459.49, -312.64) * mm, "end": v(457.15, -312.65) * mm});
            skLineSegment(sketch, "E818", {"start": v(457.15, -312.65) * mm, "end": v(457.15, -310.69) * mm});
            skLineSegment(sketch, "E819", {"start": v(457.15, -310.69) * mm, "end": v(459.48, -310.69) * mm});
            skLineSegment(sketch, "E820", {"start": v(455.29, -300.39) * mm, "end": v(455.3, -301.83) * mm});
            skLineSegment(sketch, "E821", {"start": v(455.3, -301.83) * mm, "end": v(459.48, -301.83) * mm});
            skLineSegment(sketch, "E822", {"start": v(459.48, -301.83) * mm, "end": v(459.48, -303.4) * mm});
            skLineSegment(sketch, "E823", {"start": v(459.48, -303.4) * mm, "end": v(455.3, -303.4) * mm});
            skLineSegment(sketch, "E824", {"start": v(455.3, -303.4) * mm, "end": v(455.3, -308.8) * mm});
            skLineSegment(sketch, "E825", {"start": v(455.3, -308.8) * mm, "end": v(453.58, -308.8) * mm});
            skLineSegment(sketch, "E826", {"start": v(453.58, -308.8) * mm, "end": v(447.3, -303.34) * mm});
            skLineSegment(sketch, "E827", {"start": v(447.3, -303.34) * mm, "end": v(447.3, -301.84) * mm});
            skLineSegment(sketch, "E828", {"start": v(447.3, -301.84) * mm, "end": v(453.98, -301.83) * mm});
            skLineSegment(sketch, "E829", {"start": v(453.98, -301.83) * mm, "end": v(453.98, -300.39) * mm});
            skLineSegment(sketch, "E830", {"start": v(453.98, -300.39) * mm, "end": v(455.29, -300.39) * mm});
            skLineSegment(sketch, "E831", {"start": v(453.98, -303.4) * mm, "end": v(449.22, -303.4) * mm});
            skLineSegment(sketch, "E832", {"start": v(449.22, -303.4) * mm, "end": v(453.98, -307.52) * mm});
            skLineSegment(sketch, "E833", {"start": v(453.98, -307.52) * mm, "end": v(453.98, -303.4) * mm});
            skLineSegment(sketch, "E834", {"start": v(453.4, -199.39) * mm, "end": v(453.4, -225.55) * mm});
            skLineSegment(sketch, "E835", {"start": v(453.4, -225.55) * mm, "end": v(453.4, -258.32) * mm});
            skLineSegment(sketch, "E836", {"start": v(453.4, -258.32) * mm, "end": v(453.4, -287.78) * mm});
            skLineSegment(sketch, "E837", {"start": v(484.88, -310.69) * mm, "end": v(484.89, -312.64) * mm});
            skLineSegment(sketch, "E838", {"start": v(484.89, -312.64) * mm, "end": v(482.55, -312.65) * mm});
            skLineSegment(sketch, "E839", {"start": v(482.55, -312.65) * mm, "end": v(482.55, -310.69) * mm});
            skLineSegment(sketch, "E840", {"start": v(482.55, -310.69) * mm, "end": v(484.88, -310.69) * mm});
            skLineSegment(sketch, "E841", {"start": v(478.8, -211.07) * mm, "end": v(478.8, -233.43) * mm});
            skLineSegment(sketch, "E842", {"start": v(478.8, -233.43) * mm, "end": v(478.8, -262.13) * mm});
            skLineSegment(sketch, "E843", {"start": v(478.8, -262.13) * mm, "end": v(478.8, -287.78) * mm});
            skLineSegment(sketch, "E844", {"start": v(-641.65, -213.87) * mm, "end": v(-643.6, -213.87) * mm});
            skLineSegment(sketch, "E845", {"start": v(-643.6, -213.87) * mm, "end": v(-643.6, -211.53) * mm});
            skLineSegment(sketch, "E846", {"start": v(-643.6, -211.53) * mm, "end": v(-641.65, -211.53) * mm});
            skLineSegment(sketch, "E847", {"start": v(-641.65, -211.53) * mm, "end": v(-641.65, -213.87) * mm});
            skLineSegment(sketch, "E848", {"start": v(-597.66, -207.77) * mm, "end": v(-609.35, -207.77) * mm});
            skLineSegment(sketch, "E849", {"start": v(-609.35, -207.77) * mm, "end": v(-618.49, -207.77) * mm});
            skLineSegment(sketch, "E850", {"start": v(-641.65, -198.88) * mm, "end": v(-643.6, -198.88) * mm});
            skLineSegment(sketch, "E851", {"start": v(-643.6, -198.88) * mm, "end": v(-643.6, -196.55) * mm});
            skLineSegment(sketch, "E852", {"start": v(-643.6, -196.55) * mm, "end": v(-641.65, -196.55) * mm});
            skLineSegment(sketch, "E853", {"start": v(-641.65, -196.55) * mm, "end": v(-641.65, -198.88) * mm});
            skLineSegment(sketch, "E854", {"start": v(-568.96, -192.79) * mm, "end": v(-582.42, -192.79) * mm});
            skLineSegment(sketch, "E855", {"start": v(-582.42, -192.79) * mm, "end": v(-601.98, -192.79) * mm});
            skLineSegment(sketch, "E856", {"start": v(-601.98, -192.79) * mm, "end": v(-618.49, -192.79) * mm});
            skLineSegment(sketch, "E857", {"start": v(-663.86, 266.57) * mm, "end": v(-665.3, 266.57) * mm});
            skLineSegment(sketch, "E858", {"start": v(-665.3, 266.57) * mm, "end": v(-665.3, 262.38) * mm});
            skLineSegment(sketch, "E859", {"start": v(-665.3, 262.38) * mm, "end": v(-666.88, 262.38) * mm});
            skLineSegment(sketch, "E860", {"start": v(-666.88, 262.38) * mm, "end": v(-666.88, 266.57) * mm});
            skLineSegment(sketch, "E861", {"start": v(-666.88, 266.57) * mm, "end": v(-672.26, 266.57) * mm});
            skLineSegment(sketch, "E862", {"start": v(-672.26, 266.57) * mm, "end": v(-672.26, 268.3) * mm});
            skLineSegment(sketch, "E863", {"start": v(-672.26, 268.3) * mm, "end": v(-666.81, 274.57) * mm});
            skLineSegment(sketch, "E864", {"start": v(-666.81, 274.57) * mm, "end": v(-665.3, 274.57) * mm});
            skLineSegment(sketch, "E865", {"start": v(-665.3, 274.57) * mm, "end": v(-665.3, 267.88) * mm});
            skLineSegment(sketch, "E866", {"start": v(-665.3, 267.88) * mm, "end": v(-663.86, 267.88) * mm});
            skLineSegment(sketch, "E867", {"start": v(-663.86, 267.88) * mm, "end": v(-663.86, 266.57) * mm});
            skLineSegment(sketch, "E868", {"start": v(-666.88, 267.88) * mm, "end": v(-666.88, 272.65) * mm});
            skLineSegment(sketch, "E869", {"start": v(-666.88, 272.65) * mm, "end": v(-670.99, 267.88) * mm});
            skLineSegment(sketch, "E870", {"start": v(-670.99, 267.88) * mm, "end": v(-666.88, 267.88) * mm});
            skLineSegment(sketch, "E871", {"start": v(-654.9, 272.74) * mm, "end": v(-660.17, 262.38) * mm});
            skLineSegment(sketch, "E872", {"start": v(-660.17, 262.38) * mm, "end": v(-661.92, 262.38) * mm});
            skLineSegment(sketch, "E873", {"start": v(-661.92, 262.38) * mm, "end": v(-656.33, 273.14) * mm});
            skLineSegment(sketch, "E874", {"start": v(-656.33, 273.14) * mm, "end": v(-662.64, 273.14) * mm});
            skLineSegment(sketch, "E875", {"start": v(-662.64, 273.14) * mm, "end": v(-662.64, 274.57) * mm});
            skLineSegment(sketch, "E876", {"start": v(-662.64, 274.57) * mm, "end": v(-654.9, 274.57) * mm});
            skLineSegment(sketch, "E877", {"start": v(-654.9, 274.57) * mm, "end": v(-654.9, 272.74) * mm});
            skLineSegment(sketch, "E878", {"start": v(-641.65, 262.38) * mm, "end": v(-643.6, 262.38) * mm});
            skLineSegment(sketch, "E879", {"start": v(-643.6, 262.38) * mm, "end": v(-643.6, 264.71) * mm});
            skLineSegment(sketch, "E880", {"start": v(-643.6, 264.71) * mm, "end": v(-641.65, 264.71) * mm});
            skLineSegment(sketch, "E881", {"start": v(-641.65, 264.71) * mm, "end": v(-641.65, 262.38) * mm});
            skLineSegment(sketch, "E882", {"start": v(-518.16, 268.48) * mm, "end": v(-548.39, 268.48) * mm});
            skLineSegment(sketch, "E883", {"start": v(-548.39, 268.48) * mm, "end": v(-585.22, 268.48) * mm});
            skLineSegment(sketch, "E884", {"start": v(-585.22, 268.48) * mm, "end": v(-618.49, 268.48) * mm});
            skLineSegment(sketch, "E885", {"start": v(-641.65, 287.78) * mm, "end": v(-643.6, 287.78) * mm});
            skLineSegment(sketch, "E886", {"start": v(-643.6, 287.78) * mm, "end": v(-643.6, 290.11) * mm});
            skLineSegment(sketch, "E887", {"start": v(-643.6, 290.11) * mm, "end": v(-641.65, 290.11) * mm});
            skLineSegment(sketch, "E888", {"start": v(-641.65, 290.11) * mm, "end": v(-641.65, 287.78) * mm});
            skLineSegment(sketch, "E889", {"start": v(-591.31, 293.88) * mm, "end": v(-597.15, 293.88) * mm});
            skLineSegment(sketch, "E890", {"start": v(-597.15, 293.88) * mm, "end": v(-609.35, 293.88) * mm});
            skLineSegment(sketch, "E891", {"start": v(-609.35, 293.88) * mm, "end": v(-618.49, 293.88) * mm});
            skLineSegment(sketch, "E892", {"start": v(538.69, 301.24) * mm, "end": v(536.73, 301.24) * mm});
            skLineSegment(sketch, "E893", {"start": v(536.73, 301.24) * mm, "end": v(536.73, 303.58) * mm});
            skLineSegment(sketch, "E894", {"start": v(536.73, 303.58) * mm, "end": v(538.69, 303.58) * mm});
            skLineSegment(sketch, "E895", {"start": v(538.69, 303.58) * mm, "end": v(538.69, 301.24) * mm});
            skLineSegment(sketch, "E896", {"start": v(525.44, 289.3) * mm, "end": v(520.53, 276.79) * mm});
            skLineSegment(sketch, "E897", {"start": v(520.53, 276.79) * mm, "end": v(518.88, 276.79) * mm});
            skLineSegment(sketch, "E898", {"start": v(518.88, 276.79) * mm, "end": v(520.52, 280.6) * mm});
            skLineSegment(sketch, "E899", {"start": v(520.52, 280.6) * mm, "end": v(517.2, 289.3) * mm});
            skLineSegment(sketch, "E900", {"start": v(517.2, 289.3) * mm, "end": v(518.86, 289.3) * mm});
            skLineSegment(sketch, "E901", {"start": v(518.86, 289.3) * mm, "end": v(521.35, 282.54) * mm});
            skLineSegment(sketch, "E902", {"start": v(521.35, 282.54) * mm, "end": v(523.84, 289.3) * mm});
            skLineSegment(sketch, "E903", {"start": v(523.84, 289.3) * mm, "end": v(525.44, 289.3) * mm});
            skLineSegment(sketch, "E904", {"start": v(548.22, 280.16) * mm, "end": v(546.33, 280.16) * mm});
            skLineSegment(sketch, "E905", {"start": v(546.33, 280.16) * mm, "end": v(544.11, 283.62) * mm});
            skLineSegment(sketch, "E906", {"start": v(544.11, 283.62) * mm, "end": v(541.83, 280.16) * mm});
            skLineSegment(sketch, "E907", {"start": v(541.83, 280.16) * mm, "end": v(540.09, 280.16) * mm});
            skLineSegment(sketch, "E908", {"start": v(540.09, 280.16) * mm, "end": v(543.26, 284.7) * mm});
            skLineSegment(sketch, "E909", {"start": v(543.26, 284.7) * mm, "end": v(540.12, 289.3) * mm});
            skLineSegment(sketch, "E910", {"start": v(540.12, 289.3) * mm, "end": v(542, 289.3) * mm});
            skLineSegment(sketch, "E911", {"start": v(542, 289.3) * mm, "end": v(544.21, 285.88) * mm});
            skLineSegment(sketch, "E912", {"start": v(544.21, 285.88) * mm, "end": v(546.47, 289.3) * mm});
            skLineSegment(sketch, "E913", {"start": v(546.47, 289.3) * mm, "end": v(548.22, 289.3) * mm});
            skLineSegment(sketch, "E914", {"start": v(548.22, 289.3) * mm, "end": v(545.06, 284.8) * mm});
            skLineSegment(sketch, "E915", {"start": v(545.06, 284.8) * mm, "end": v(548.22, 280.16) * mm});
            skLineSegment(sketch, "E916", {"start": v(562.2, 284.35) * mm, "end": v(560.75, 284.35) * mm});
            skLineSegment(sketch, "E917", {"start": v(560.75, 284.35) * mm, "end": v(560.75, 280.16) * mm});
            skLineSegment(sketch, "E918", {"start": v(560.75, 280.16) * mm, "end": v(559.18, 280.16) * mm});
            skLineSegment(sketch, "E919", {"start": v(559.18, 280.16) * mm, "end": v(559.18, 284.35) * mm});
            skLineSegment(sketch, "E920", {"start": v(559.18, 284.35) * mm, "end": v(553.8, 284.35) * mm});
            skLineSegment(sketch, "E921", {"start": v(553.8, 284.35) * mm, "end": v(553.8, 286.07) * mm});
            skLineSegment(sketch, "E922", {"start": v(553.8, 286.07) * mm, "end": v(559.24, 292.35) * mm});
            skLineSegment(sketch, "E923", {"start": v(559.24, 292.35) * mm, "end": v(560.75, 292.35) * mm});
            skLineSegment(sketch, "E924", {"start": v(560.75, 292.35) * mm, "end": v(560.75, 285.66) * mm});
            skLineSegment(sketch, "E925", {"start": v(560.75, 285.66) * mm, "end": v(562.2, 285.66) * mm});
            skLineSegment(sketch, "E926", {"start": v(562.2, 285.66) * mm, "end": v(562.2, 284.35) * mm});
            skLineSegment(sketch, "E927", {"start": v(559.18, 285.66) * mm, "end": v(559.18, 290.43) * mm});
            skLineSegment(sketch, "E928", {"start": v(559.18, 290.43) * mm, "end": v(555.07, 285.66) * mm});
            skLineSegment(sketch, "E929", {"start": v(555.07, 285.66) * mm, "end": v(559.18, 285.66) * mm});
            skLineSegment(sketch, "E930", {"start": v(484.12, 300.74) * mm, "end": v(477.77, 293.12) * mm});
            skLineSegment(sketch, "E931", {"start": v(482.6, 302) * mm, "end": v(477.77, 293.12) * mm});
            skLineSegment(sketch, "E932", {"start": v(477.77, 293.12) * mm, "end": v(485.65, 299.47) * mm});
            skLineSegment(sketch, "E933", {"start": v(485.65, 299.47) * mm, "end": v(482.6, 302) * mm});
            skLineSegment(sketch, "E934", {"start": v(484.12, 300.74) * mm, "end": v(489.97, 307.34) * mm});
            skLineSegment(sketch, "E935", {"start": v(489.97, 307.34) * mm, "end": v(501.9, 307.34) * mm});
            skLineSegment(sketch, "E936", {"start": v(16.51, 241.07) * mm, "end": v(24.51, 241.07) * mm});
            skLineSegment(sketch, "E937", {"start": v(24.51, 241.07) * mm, "end": v(24.51, 229.87) * mm});
            skLineSegment(sketch, "E938", {"start": v(24.51, 229.87) * mm, "end": v(16.51, 229.87) * mm});
            skLineSegment(sketch, "E939", {"start": v(16.51, 229.87) * mm, "end": v(16.51, 241.07) * mm});
            skLineSegment(sketch, "E940", {"start": v(17.31, 231.4) * mm, "end": v(20.03, 235.47) * mm});
            skLineSegment(sketch, "E941", {"start": v(20.03, 235.47) * mm, "end": v(17.31, 239.55) * mm});
            skLineSegment(sketch, "E942", {"start": v(17.31, 239.55) * mm, "end": v(17.31, 231.4) * mm});
            skLineSegment(sketch, "E943", {"start": v(23.23, 240.27) * mm, "end": v(17.8, 240.27) * mm});
            skLineSegment(sketch, "E944", {"start": v(17.8, 240.27) * mm, "end": v(20.51, 236.2) * mm});
            skLineSegment(sketch, "E945", {"start": v(20.51, 236.2) * mm, "end": v(23.23, 240.27) * mm});
            skLineSegment(sketch, "E946", {"start": v(23.23, 230.67) * mm, "end": v(20.51, 234.75) * mm});
            skLineSegment(sketch, "E947", {"start": v(20.51, 234.75) * mm, "end": v(17.8, 230.67) * mm});
            skLineSegment(sketch, "E948", {"start": v(17.8, 230.67) * mm, "end": v(23.23, 230.67) * mm});
            skLineSegment(sketch, "E949", {"start": v(23.71, 231.4) * mm, "end": v(23.71, 239.55) * mm});
            skLineSegment(sketch, "E950", {"start": v(23.71, 239.55) * mm, "end": v(21, 235.47) * mm});
            skLineSegment(sketch, "E951", {"start": v(21, 235.47) * mm, "end": v(23.71, 231.4) * mm});
            skLineSegment(sketch, "E952", {"start": v(33.74, 229.87) * mm, "end": v(31.78, 229.87) * mm});
            skLineSegment(sketch, "E953", {"start": v(31.78, 229.87) * mm, "end": v(31.78, 232.2) * mm});
            skLineSegment(sketch, "E954", {"start": v(31.78, 232.2) * mm, "end": v(33.74, 232.2) * mm});
            skLineSegment(sketch, "E955", {"start": v(33.74, 232.2) * mm, "end": v(33.74, 229.87) * mm});
            skLineSegment(sketch, "E956", {"start": v(63.01, 229.87) * mm, "end": v(63.01, 240.62) * mm});
            skLineSegment(sketch, "E957", {"start": v(63.01, 240.62) * mm, "end": v(58.92, 240.62) * mm});
            skLineSegment(sketch, "E958", {"start": v(58.92, 240.62) * mm, "end": v(58.92, 242.06) * mm});
            skLineSegment(sketch, "E959", {"start": v(58.92, 242.06) * mm, "end": v(68.73, 242.06) * mm});
            skLineSegment(sketch, "E960", {"start": v(68.73, 242.06) * mm, "end": v(68.73, 240.62) * mm});
            skLineSegment(sketch, "E961", {"start": v(68.73, 240.62) * mm, "end": v(64.63, 240.62) * mm});
            skLineSegment(sketch, "E962", {"start": v(64.63, 240.62) * mm, "end": v(64.63, 229.87) * mm});
            skLineSegment(sketch, "E963", {"start": v(64.63, 229.87) * mm, "end": v(63.01, 229.87) * mm});
            skLineSegment(sketch, "E964", {"start": v(78.66, 229.87) * mm, "end": v(77.04, 229.87) * mm});
            skLineSegment(sketch, "E965", {"start": v(77.04, 229.87) * mm, "end": v(77.04, 235.84) * mm});
            skLineSegment(sketch, "E966", {"start": v(77.04, 235.84) * mm, "end": v(71.44, 235.84) * mm});
            skLineSegment(sketch, "E967", {"start": v(71.44, 235.84) * mm, "end": v(71.44, 229.87) * mm});
            skLineSegment(sketch, "E968", {"start": v(71.44, 229.87) * mm, "end": v(69.82, 229.87) * mm});
            skLineSegment(sketch, "E969", {"start": v(69.82, 229.87) * mm, "end": v(69.82, 242.06) * mm});
            skLineSegment(sketch, "E970", {"start": v(69.82, 242.06) * mm, "end": v(71.44, 242.06) * mm});
            skLineSegment(sketch, "E971", {"start": v(71.44, 242.06) * mm, "end": v(71.44, 237.28) * mm});
            skLineSegment(sketch, "E972", {"start": v(71.44, 237.28) * mm, "end": v(77.04, 237.28) * mm});
            skLineSegment(sketch, "E973", {"start": v(77.04, 237.28) * mm, "end": v(77.04, 242.06) * mm});
            skLineSegment(sketch, "E974", {"start": v(77.04, 242.06) * mm, "end": v(78.66, 242.06) * mm});
            skLineSegment(sketch, "E975", {"start": v(78.66, 242.06) * mm, "end": v(78.66, 229.87) * mm});
            skLineSegment(sketch, "E976", {"start": v(16.51, 219.74) * mm, "end": v(24.51, 219.74) * mm});
            skLineSegment(sketch, "E977", {"start": v(24.51, 219.74) * mm, "end": v(24.51, 208.53) * mm});
            skLineSegment(sketch, "E978", {"start": v(24.51, 208.53) * mm, "end": v(16.51, 208.53) * mm});
            skLineSegment(sketch, "E979", {"start": v(16.51, 208.53) * mm, "end": v(16.51, 219.74) * mm});
            skLineSegment(sketch, "E980", {"start": v(17.31, 210.05) * mm, "end": v(20.03, 214.14) * mm});
            skLineSegment(sketch, "E981", {"start": v(20.03, 214.14) * mm, "end": v(17.31, 218.22) * mm});
            skLineSegment(sketch, "E982", {"start": v(17.31, 218.22) * mm, "end": v(17.31, 210.05) * mm});
            skLineSegment(sketch, "E983", {"start": v(23.23, 218.94) * mm, "end": v(17.8, 218.94) * mm});
            skLineSegment(sketch, "E984", {"start": v(17.8, 218.94) * mm, "end": v(20.51, 214.86) * mm});
            skLineSegment(sketch, "E985", {"start": v(20.51, 214.86) * mm, "end": v(23.23, 218.94) * mm});
            skLineSegment(sketch, "E986", {"start": v(23.23, 209.33) * mm, "end": v(20.51, 213.42) * mm});
            skLineSegment(sketch, "E987", {"start": v(20.51, 213.42) * mm, "end": v(17.8, 209.33) * mm});
            skLineSegment(sketch, "E988", {"start": v(17.8, 209.33) * mm, "end": v(23.23, 209.33) * mm});
            skLineSegment(sketch, "E989", {"start": v(23.71, 210.05) * mm, "end": v(23.71, 218.22) * mm});
            skLineSegment(sketch, "E990", {"start": v(23.71, 218.22) * mm, "end": v(21, 214.14) * mm});
            skLineSegment(sketch, "E991", {"start": v(21, 214.14) * mm, "end": v(23.71, 210.05) * mm});
            skLineSegment(sketch, "E992", {"start": v(48.26, 219.74) * mm, "end": v(56.26, 219.74) * mm});
            skLineSegment(sketch, "E993", {"start": v(56.26, 219.74) * mm, "end": v(56.26, 208.53) * mm});
            skLineSegment(sketch, "E994", {"start": v(56.26, 208.53) * mm, "end": v(48.26, 208.53) * mm});
            skLineSegment(sketch, "E995", {"start": v(48.26, 208.53) * mm, "end": v(48.26, 219.74) * mm});
            skLineSegment(sketch, "E996", {"start": v(49.06, 210.05) * mm, "end": v(51.78, 214.14) * mm});
            skLineSegment(sketch, "E997", {"start": v(51.78, 214.14) * mm, "end": v(49.06, 218.22) * mm});
            skLineSegment(sketch, "E998", {"start": v(49.06, 218.22) * mm, "end": v(49.06, 210.05) * mm});
            skLineSegment(sketch, "E999", {"start": v(54.98, 218.94) * mm, "end": v(49.54, 218.94) * mm});
            skLineSegment(sketch, "E1000", {"start": v(49.54, 218.94) * mm, "end": v(52.26, 214.86) * mm});
            skLineSegment(sketch, "E1001", {"start": v(52.26, 214.86) * mm, "end": v(54.98, 218.94) * mm});
            skLineSegment(sketch, "E1002", {"start": v(54.98, 209.33) * mm, "end": v(52.26, 213.42) * mm});
            skLineSegment(sketch, "E1003", {"start": v(52.26, 213.42) * mm, "end": v(49.54, 209.33) * mm});
            skLineSegment(sketch, "E1004", {"start": v(49.54, 209.33) * mm, "end": v(54.98, 209.33) * mm});
            skLineSegment(sketch, "E1005", {"start": v(55.46, 210.05) * mm, "end": v(55.46, 218.22) * mm});
            skLineSegment(sketch, "E1006", {"start": v(55.46, 218.22) * mm, "end": v(52.74, 214.14) * mm});
            skLineSegment(sketch, "E1007", {"start": v(52.74, 214.14) * mm, "end": v(55.46, 210.05) * mm});
            skLineSegment(sketch, "E1008", {"start": v(65.49, 208.53) * mm, "end": v(63.53, 208.53) * mm});
            skLineSegment(sketch, "E1009", {"start": v(63.53, 208.53) * mm, "end": v(63.53, 210.87) * mm});
            skLineSegment(sketch, "E1010", {"start": v(63.53, 210.87) * mm, "end": v(65.49, 210.87) * mm});
            skLineSegment(sketch, "E1011", {"start": v(65.49, 210.87) * mm, "end": v(65.49, 208.53) * mm});
            skLineSegment(sketch, "E1012", {"start": v(90.42, 219.74) * mm, "end": v(98.43, 219.74) * mm});
            skLineSegment(sketch, "E1013", {"start": v(98.43, 219.74) * mm, "end": v(98.43, 208.53) * mm});
            skLineSegment(sketch, "E1014", {"start": v(98.43, 208.53) * mm, "end": v(90.42, 208.53) * mm});
            skLineSegment(sketch, "E1015", {"start": v(90.42, 208.53) * mm, "end": v(90.42, 219.74) * mm});
            skLineSegment(sketch, "E1016", {"start": v(91.22, 210.05) * mm, "end": v(93.94, 214.14) * mm});
            skLineSegment(sketch, "E1017", {"start": v(93.94, 214.14) * mm, "end": v(91.22, 218.22) * mm});
            skLineSegment(sketch, "E1018", {"start": v(91.22, 218.22) * mm, "end": v(91.22, 210.05) * mm});
            skLineSegment(sketch, "E1019", {"start": v(97.15, 218.94) * mm, "end": v(91.7, 218.94) * mm});
            skLineSegment(sketch, "E1020", {"start": v(91.7, 218.94) * mm, "end": v(94.42, 214.86) * mm});
            skLineSegment(sketch, "E1021", {"start": v(94.42, 214.86) * mm, "end": v(97.15, 218.94) * mm});
            skLineSegment(sketch, "E1022", {"start": v(97.15, 209.33) * mm, "end": v(94.42, 213.42) * mm});
            skLineSegment(sketch, "E1023", {"start": v(94.42, 213.42) * mm, "end": v(91.7, 209.33) * mm});
            skLineSegment(sketch, "E1024", {"start": v(91.7, 209.33) * mm, "end": v(97.15, 209.33) * mm});
            skLineSegment(sketch, "E1025", {"start": v(97.63, 210.05) * mm, "end": v(97.63, 218.22) * mm});
            skLineSegment(sketch, "E1026", {"start": v(97.63, 218.22) * mm, "end": v(94.9, 214.14) * mm});
            skLineSegment(sketch, "E1027", {"start": v(94.9, 214.14) * mm, "end": v(97.63, 210.05) * mm});
            skLineSegment(sketch, "E1028", {"start": v(113.5, 208.53) * mm, "end": v(111.54, 208.53) * mm});
            skLineSegment(sketch, "E1029", {"start": v(111.54, 208.53) * mm, "end": v(111.54, 210.87) * mm});
            skLineSegment(sketch, "E1030", {"start": v(111.54, 210.87) * mm, "end": v(113.5, 210.87) * mm});
            skLineSegment(sketch, "E1031", {"start": v(113.5, 210.87) * mm, "end": v(113.5, 208.53) * mm});
            skLineSegment(sketch, "E1032", {"start": v(36.75, 196.34) * mm, "end": v(31.83, 183.83) * mm});
            skLineSegment(sketch, "E1033", {"start": v(31.83, 183.83) * mm, "end": v(30.18, 183.83) * mm});
            skLineSegment(sketch, "E1034", {"start": v(30.18, 183.83) * mm, "end": v(31.82, 187.64) * mm});
            skLineSegment(sketch, "E1035", {"start": v(31.82, 187.64) * mm, "end": v(28.5, 196.34) * mm});
            skLineSegment(sketch, "E1036", {"start": v(28.5, 196.34) * mm, "end": v(30.16, 196.34) * mm});
            skLineSegment(sketch, "E1037", {"start": v(30.16, 196.34) * mm, "end": v(32.66, 189.57) * mm});
            skLineSegment(sketch, "E1038", {"start": v(32.66, 189.57) * mm, "end": v(35.14, 196.34) * mm});
            skLineSegment(sketch, "E1039", {"start": v(35.14, 196.34) * mm, "end": v(36.75, 196.34) * mm});
            skLineSegment(sketch, "E1040", {"start": v(49.74, 187.2) * mm, "end": v(47.78, 187.2) * mm});
            skLineSegment(sketch, "E1041", {"start": v(47.78, 187.2) * mm, "end": v(47.78, 189.53) * mm});
            skLineSegment(sketch, "E1042", {"start": v(47.78, 189.53) * mm, "end": v(49.74, 189.53) * mm});
            skLineSegment(sketch, "E1043", {"start": v(49.74, 189.53) * mm, "end": v(49.74, 187.2) * mm});
            skLineSegment(sketch, "E1044", {"start": v(64.6, 187.2) * mm, "end": v(62.72, 187.2) * mm});
            skLineSegment(sketch, "E1045", {"start": v(62.72, 187.2) * mm, "end": v(60.5, 190.65) * mm});
            skLineSegment(sketch, "E1046", {"start": v(60.5, 190.65) * mm, "end": v(58.21, 187.2) * mm});
            skLineSegment(sketch, "E1047", {"start": v(58.21, 187.2) * mm, "end": v(56.47, 187.2) * mm});
            skLineSegment(sketch, "E1048", {"start": v(56.47, 187.2) * mm, "end": v(59.65, 191.73) * mm});
            skLineSegment(sketch, "E1049", {"start": v(59.65, 191.73) * mm, "end": v(56.5, 196.34) * mm});
            skLineSegment(sketch, "E1050", {"start": v(56.5, 196.34) * mm, "end": v(58.4, 196.34) * mm});
            skLineSegment(sketch, "E1051", {"start": v(58.4, 196.34) * mm, "end": v(60.6, 192.92) * mm});
            skLineSegment(sketch, "E1052", {"start": v(60.6, 192.92) * mm, "end": v(62.85, 196.34) * mm});
            skLineSegment(sketch, "E1053", {"start": v(62.85, 196.34) * mm, "end": v(64.6, 196.34) * mm});
            skLineSegment(sketch, "E1054", {"start": v(64.6, 196.34) * mm, "end": v(61.45, 191.84) * mm});
            skLineSegment(sketch, "E1055", {"start": v(61.45, 191.84) * mm, "end": v(64.6, 187.2) * mm});
            skLineSegment(sketch, "E1056", {"start": v(-40.39, 260.1) * mm, "end": v(-49.02, 265.18) * mm});
            skLineSegment(sketch, "E1057", {"start": v(-39.37, 261.87) * mm, "end": v(-49.02, 265.18) * mm});
            skLineSegment(sketch, "E1058", {"start": v(-49.02, 265.18) * mm, "end": v(-41.4, 258.57) * mm});
            skLineSegment(sketch, "E1059", {"start": v(-41.4, 258.57) * mm, "end": v(-39.37, 261.87) * mm});
            skLineSegment(sketch, "E1060", {"start": v(-40.39, 260.1) * mm, "end": v(1.27, 235.97) * mm});
            skLineSegment(sketch, "E1061", {"start": v(1.27, 235.97) * mm, "end": v(13.2, 235.97) * mm});
            skLineSegment(sketch, "E1062", {"start": v(-584.96, 42.93) * mm, "end": v(-540, 42.93) * mm});
            skLineSegment(sketch, "E1063", {"start": v(-528.07, 42.93) * mm, "end": v(-512.06, 42.93) * mm});
            skLineSegment(sketch, "E1064", {"start": v(-500.13, 42.93) * mm, "end": v(-455.42, 42.93) * mm});
            skLineSegment(sketch, "E1065", {"start": v(-443.48, 42.93) * mm, "end": v(-427.48, 42.93) * mm});
            skLineSegment(sketch, "E1066", {"start": v(-415.54, 42.93) * mm, "end": v(-370.84, 42.93) * mm});
            skLineSegment(sketch, "E1067", {"start": v(-358.9, 42.93) * mm, "end": v(-342.9, 42.93) * mm});
            skLineSegment(sketch, "E1068", {"start": v(-330.96, 42.93) * mm, "end": v(-286.26, 42.93) * mm});
            skLineSegment(sketch, "E1069", {"start": v(-274.32, 42.93) * mm, "end": v(-258.32, 42.93) * mm});
            skLineSegment(sketch, "E1070", {"start": v(-246.38, 42.93) * mm, "end": v(-201.42, 42.93) * mm});
            skLineSegment(sketch, "E1071", {"start": v(-189.48, 42.93) * mm, "end": v(-173.48, 42.93) * mm});
            skLineSegment(sketch, "E1072", {"start": v(-161.54, 42.93) * mm, "end": v(-116.84, 42.93) * mm});
            skLineSegment(sketch, "E1073", {"start": v(-104.9, 42.93) * mm, "end": v(-88.9, 42.93) * mm});
            skLineSegment(sketch, "E1074", {"start": v(-76.96, 42.93) * mm, "end": v(-32.26, 42.93) * mm});
            skLineSegment(sketch, "E1075", {"start": v(-20.32, 42.93) * mm, "end": v(-4.32, 42.93) * mm});
            skLineSegment(sketch, "E1076", {"start": v(7.62, 42.93) * mm, "end": v(52.32, 42.93) * mm});
            skLineSegment(sketch, "E1077", {"start": v(64.26, 42.93) * mm, "end": v(80.26, 42.93) * mm});
            skLineSegment(sketch, "E1078", {"start": v(92.2, 42.93) * mm, "end": v(136.9, 42.93) * mm});
            skLineSegment(sketch, "E1079", {"start": v(149.1, 42.93) * mm, "end": v(164.85, 42.93) * mm});
            skLineSegment(sketch, "E1080", {"start": v(177.04, 42.93) * mm, "end": v(221.74, 42.93) * mm});
            skLineSegment(sketch, "E1081", {"start": v(233.68, 42.93) * mm, "end": v(249.68, 42.93) * mm});
            skLineSegment(sketch, "E1082", {"start": v(261.62, 42.93) * mm, "end": v(306.32, 42.93) * mm});
            skLineSegment(sketch, "E1083", {"start": v(318.26, 42.93) * mm, "end": v(334.26, 42.93) * mm});
            skLineSegment(sketch, "E1084", {"start": v(346.2, 42.93) * mm, "end": v(390.9, 42.93) * mm});
            skLineSegment(sketch, "E1085", {"start": v(402.84, 42.93) * mm, "end": v(418.85, 42.93) * mm});
            skLineSegment(sketch, "E1086", {"start": v(430.78, 42.93) * mm, "end": v(475.49, 42.93) * mm});
            skLineSegment(sketch, "E1087", {"start": v(-597.66, 42.93) * mm, "end": v(-584.96, 42.93) * mm});
            skLineSegment(sketch, "E1088", {"start": v(475.49, 42.93) * mm, "end": v(488.19, 42.93) * mm});
            skLineSegment(sketch, "E1089", {"start": v(-54.61, -204.72) * mm, "end": v(-54.61, -155.45) * mm});
            skLineSegment(sketch, "E1090", {"start": v(-54.61, -143.51) * mm, "end": v(-54.61, -127.5) * mm});
            skLineSegment(sketch, "E1091", {"start": v(-54.61, -115.57) * mm, "end": v(-54.61, -66.3) * mm});
            skLineSegment(sketch, "E1092", {"start": v(-54.61, -54.36) * mm, "end": v(-54.61, -38.35) * mm});
            skLineSegment(sketch, "E1093", {"start": v(-54.61, -26.42) * mm, "end": v(-54.61, 22.86) * mm});
            skLineSegment(sketch, "E1094", {"start": v(-54.61, 35.05) * mm, "end": v(-54.61, 50.8) * mm});
            skLineSegment(sketch, "E1095", {"start": v(-54.61, 63) * mm, "end": v(-54.61, 112.27) * mm});
            skLineSegment(sketch, "E1096", {"start": v(-54.61, 124.2) * mm, "end": v(-54.61, 140.2) * mm});
            skLineSegment(sketch, "E1097", {"start": v(-54.61, 152.15) * mm, "end": v(-54.61, 201.42) * mm});
            skLineSegment(sketch, "E1098", {"start": v(-54.61, 213.36) * mm, "end": v(-54.61, 229.36) * mm});
            skLineSegment(sketch, "E1099", {"start": v(-54.61, 241.3) * mm, "end": v(-54.61, 290.58) * mm});
            skLineSegment(sketch, "E1100", {"start": v(-54.61, -217.42) * mm, "end": v(-54.61, -204.72) * mm});
            skLineSegment(sketch, "E1101", {"start": v(-54.61, 290.58) * mm, "end": v(-54.61, 303.28) * mm});
            skSolve(sketch);
        }
        {
            var Q0;
            Q0=qCreatedBy(makeId("Top.planeOp"),FACE);
            var sketch = newSketch(context, id + "F1", { "sketchPlane" : qUnion([Q0])});
            skLineSegment(sketch, "E1102.0", {"start": v(-588.01, -204.72) * mm, "end": v(-588.01, 290.58) * mm, "construction": true});
            skFitSpline(sketch, "E1103.0", {"points": [v(-584.83, 293.88) * mm, v(-586.59, 293.88) * mm, v(-588, 292.46) * mm, v(-588.01, 290.7) * mm], "construction": true});
            skLineSegment(sketch, "E1104.0", {"start": v(-584.96, 293.88) * mm, "end": v(475.49, 293.88) * mm, "construction": true});
            skFitSpline(sketch, "E1105.0", {"points": [v(478.8, 290.7) * mm, v(478.8, 292.46) * mm, v(477.37, 293.88) * mm, v(475.62, 293.88) * mm], "construction": true});
            skLineSegment(sketch, "E1106.0", {"start": v(478.8, 290.58) * mm, "end": v(478.8, -204.72) * mm, "construction": true});
            skFitSpline(sketch, "E1107.0", {"points": [v(475.61, -207.77) * mm, v(477.37, -207.77) * mm, v(478.79, -206.35) * mm, v(478.8, -204.6) * mm], "construction": true});
            skLineSegment(sketch, "E1108.0", {"start": v(475.49, -207.77) * mm, "end": v(-584.96, -207.77) * mm, "construction": true});
            skFitSpline(sketch, "E1109.0", {"points": [v(-588.01, -204.6) * mm, v(-588.01, -206.35) * mm, v(-586.59, -207.77) * mm, v(-584.84, -207.77) * mm], "construction": true});
            skPoint(sketch, "E1110.0", {"position": v(-568.96, -192.79) * mm});
            skPoint(sketch, "E1111.0", {"position": v(-562.61, -199.39) * mm});
            skPoint(sketch, "E1112.0", {"position": v(-461.01, -199.39) * mm});
            skPoint(sketch, "E1113.0", {"position": v(-105.41, -199.39) * mm});
            skPoint(sketch, "E1114.0", {"position": v(-3.81, -199.39) * mm});
            skPoint(sketch, "E1115.0", {"position": v(351.8, -199.39) * mm});
            skPoint(sketch, "E1116.0", {"position": v(453.4, -199.39) * mm});
            skPoint(sketch, "E1117.0", {"position": v(402.6, 261.87) * mm});
            skPoint(sketch, "E1118.0", {"position": v(-54.61, 265.94) * mm});
            skPoint(sketch, "E1119.0", {"position": v(-518.16, 268.48) * mm});
            skPoint(sketch, "E1120.0", {"position": v(-511.81, 261.87) * mm});
            skLineSegment(sketch, "E1121.0", {"start": v(-511.81, 261.87) * mm, "end": v(-511.81, 82.04) * mm, "construction": true});
            skLineSegment(sketch, "E1122.0", {"start": v(-511.81, 82.04) * mm, "end": v(-511.81, 43.43) * mm, "construction": true});
            skLineSegment(sketch, "E1122.1", {"start": v(-511.81, 42.42) * mm, "end": v(-511.81, -104.4) * mm, "construction": true});
            skLineSegment(sketch, "E1122.2", {"start": v(-568.96, -192.79) * mm, "end": v(-582.42, -192.79) * mm, "construction": true});
            skLineSegment(sketch, "E1122.3", {"start": v(-562.61, -199.39) * mm, "end": v(-562.61, -225.55) * mm, "construction": true});
            skLineSegment(sketch, "E1122.4", {"start": v(-461.01, -199.39) * mm, "end": v(-461.01, -225.55) * mm, "construction": true});
            skLineSegment(sketch, "E1122.5", {"start": v(-511.81, -104.4) * mm, "end": v(-511.81, -287.78) * mm, "construction": true});
            skLineSegment(sketch, "E1122.6", {"start": v(-105.41, -199.39) * mm, "end": v(-105.41, -225.55) * mm, "construction": true});
            skLineSegment(sketch, "E1122.7", {"start": v(-54.61, -204.72) * mm, "end": v(-54.61, -155.45) * mm, "construction": true});
            skLineSegment(sketch, "E1122.8", {"start": v(-54.61, -217.42) * mm, "end": v(-54.61, -204.72) * mm, "construction": true});
            skLineSegment(sketch, "E1122.9", {"start": v(-54.61, -217.42) * mm, "end": v(-54.61, -287.78) * mm, "construction": true});
            skLineSegment(sketch, "E1122.10", {"start": v(-3.81, -199.39) * mm, "end": v(-3.81, -225.55) * mm, "construction": true});
            skLineSegment(sketch, "E1122.11", {"start": v(351.8, -199.39) * mm, "end": v(351.8, -225.55) * mm, "construction": true});
            skLineSegment(sketch, "E1122.12", {"start": v(453.4, -199.39) * mm, "end": v(453.4, -225.55) * mm, "construction": true});
            skLineSegment(sketch, "E1122.13", {"start": v(402.6, -104.4) * mm, "end": v(402.6, -287.78) * mm, "construction": true});
            skLineSegment(sketch, "E1122.14", {"start": v(402.6, 42.42) * mm, "end": v(402.6, -104.4) * mm, "construction": true});
            skLineSegment(sketch, "E1122.15", {"start": v(402.6, 82.04) * mm, "end": v(402.6, 43.43) * mm, "construction": true});
            skLineSegment(sketch, "E1122.16", {"start": v(402.6, 261.87) * mm, "end": v(402.6, 82.04) * mm, "construction": true});
            skLineSegment(sketch, "E1123.0", {"start": v(-54.61, 241.3) * mm, "end": v(-54.61, 290.58) * mm, "construction": true});
            skLineSegment(sketch, "E1124.0", {"start": v(-54.61, 290.58) * mm, "end": v(-54.61, 303.28) * mm, "construction": true});
            skLineSegment(sketch, "E1125.0", {"start": v(-518.16, 268.48) * mm, "end": v(-548.39, 268.48) * mm, "construction": true});
            skLineSegment(sketch, "E1126.0", {"start": v(-548.39, 268.48) * mm, "end": v(-585.22, 268.48) * mm, "construction": true});
            skLineSegment(sketch, "E1127.0", {"start": v(-585.22, 268.48) * mm, "end": v(-618.49, 268.48) * mm, "construction": true});
            skLineSegment(sketch, "E1128.0", {"start": v(-597.15, 293.88) * mm, "end": v(-609.35, 293.88) * mm, "construction": true});
            skLineSegment(sketch, "E1129.0", {"start": v(-591.31, 293.88) * mm, "end": v(-597.15, 293.88) * mm, "construction": true});
            skLineSegment(sketch, "E1130.0", {"start": v(-588.01, 296.93) * mm, "end": v(-588.01, 391.41) * mm, "construction": true});
            skLineSegment(sketch, "E1131.0", {"start": v(-609.35, 293.88) * mm, "end": v(-618.49, 293.88) * mm, "construction": true});
            skLineSegment(sketch, "E1132.0", {"start": v(-54.61, 213.36) * mm, "end": v(-54.61, 229.36) * mm, "construction": true});
            skLineSegment(sketch, "E1133.0", {"start": v(-54.61, 152.15) * mm, "end": v(-54.61, 201.42) * mm, "construction": true});
            skLineSegment(sketch, "E1134.0", {"start": v(-54.61, 124.2) * mm, "end": v(-54.61, 140.2) * mm, "construction": true});
            skLineSegment(sketch, "E1135.0", {"start": v(-54.61, 63) * mm, "end": v(-54.61, 112.27) * mm, "construction": true});
            skLineSegment(sketch, "E1136.0", {"start": v(-54.61, 35.05) * mm, "end": v(-54.61, 50.8) * mm, "construction": true});
            skLineSegment(sketch, "E1137.0", {"start": v(-54.61, -26.42) * mm, "end": v(-54.61, 22.86) * mm, "construction": true});
            skLineSegment(sketch, "E1138.0", {"start": v(-54.61, -143.51) * mm, "end": v(-54.61, -127.5) * mm, "construction": true});
            skLineSegment(sketch, "E1139.0", {"start": v(-54.61, -115.57) * mm, "end": v(-54.61, -66.3) * mm, "construction": true});
            skLineSegment(sketch, "E1140.0", {"start": v(-54.61, -54.36) * mm, "end": v(-54.61, -38.35) * mm, "construction": true});
            skLineSegment(sketch, "E1141.0", {"start": v(-584.96, 42.93) * mm, "end": v(-540, 42.93) * mm, "construction": true});
            skLineSegment(sketch, "E1142.0", {"start": v(-528.07, 42.93) * mm, "end": v(-512.06, 42.93) * mm, "construction": true});
            skLineSegment(sketch, "E1143.0", {"start": v(-500.13, 42.93) * mm, "end": v(-455.42, 42.93) * mm, "construction": true});
            skLineSegment(sketch, "E1144.0", {"start": v(-443.48, 42.93) * mm, "end": v(-427.48, 42.93) * mm, "construction": true});
            skLineSegment(sketch, "E1145.0", {"start": v(-415.54, 42.93) * mm, "end": v(-370.84, 42.93) * mm, "construction": true});
            skLineSegment(sketch, "E1146.0", {"start": v(-358.9, 42.93) * mm, "end": v(-342.9, 42.93) * mm, "construction": true});
            skLineSegment(sketch, "E1147.0", {"start": v(-330.96, 42.93) * mm, "end": v(-286.26, 42.93) * mm, "construction": true});
            skLineSegment(sketch, "E1148.0", {"start": v(-274.32, 42.93) * mm, "end": v(-258.32, 42.93) * mm, "construction": true});
            skLineSegment(sketch, "E1149.0", {"start": v(-246.38, 42.93) * mm, "end": v(-201.42, 42.93) * mm, "construction": true});
            skLineSegment(sketch, "E1150.0", {"start": v(-189.48, 42.93) * mm, "end": v(-173.48, 42.93) * mm, "construction": true});
            skLineSegment(sketch, "E1151.0", {"start": v(-161.54, 42.93) * mm, "end": v(-116.84, 42.93) * mm, "construction": true});
            skLineSegment(sketch, "E1152.0", {"start": v(-104.9, 42.93) * mm, "end": v(-88.9, 42.93) * mm, "construction": true});
            skLineSegment(sketch, "E1153.0", {"start": v(-76.96, 42.93) * mm, "end": v(-32.26, 42.93) * mm, "construction": true});
            skLineSegment(sketch, "E1154.0", {"start": v(-20.32, 42.93) * mm, "end": v(-4.32, 42.93) * mm, "construction": true});
            skLineSegment(sketch, "E1155.0", {"start": v(7.62, 42.93) * mm, "end": v(52.32, 42.93) * mm, "construction": true});
            skLineSegment(sketch, "E1156.0", {"start": v(64.26, 42.93) * mm, "end": v(80.26, 42.93) * mm, "construction": true});
            skLineSegment(sketch, "E1157.0", {"start": v(92.2, 42.93) * mm, "end": v(136.9, 42.93) * mm, "construction": true});
            skLineSegment(sketch, "E1158.0", {"start": v(149.1, 42.93) * mm, "end": v(164.85, 42.93) * mm, "construction": true});
            skLineSegment(sketch, "E1159.0", {"start": v(177.04, 42.93) * mm, "end": v(221.74, 42.93) * mm, "construction": true});
            skLineSegment(sketch, "E1160.0", {"start": v(233.68, 42.93) * mm, "end": v(249.68, 42.93) * mm, "construction": true});
            skLineSegment(sketch, "E1161.0", {"start": v(261.62, 42.93) * mm, "end": v(306.32, 42.93) * mm, "construction": true});
            skLineSegment(sketch, "E1162.0", {"start": v(318.26, 42.93) * mm, "end": v(334.26, 42.93) * mm, "construction": true});
            skLineSegment(sketch, "E1163.0", {"start": v(346.2, 42.93) * mm, "end": v(390.9, 42.93) * mm, "construction": true});
            skLineSegment(sketch, "E1164.0", {"start": v(402.84, 42.93) * mm, "end": v(418.85, 42.93) * mm, "construction": true});
            skLineSegment(sketch, "E1165.0", {"start": v(430.78, 42.93) * mm, "end": v(475.49, 42.93) * mm, "construction": true});
            skLineSegment(sketch, "E1166.0", {"start": v(475.49, 42.93) * mm, "end": v(488.19, 42.93) * mm, "construction": true});
            skLineSegment(sketch, "E1167.0", {"start": v(-588.01, -233.43) * mm, "end": v(-588.01, -262.13) * mm, "construction": true});
            skLineSegment(sketch, "E1168.0", {"start": v(-588.01, -262.13) * mm, "end": v(-588.01, -287.78) * mm, "construction": true});
            skLineSegment(sketch, "E1169.0", {"start": v(-562.61, -258.32) * mm, "end": v(-562.61, -287.78) * mm, "construction": true});
            skLineSegment(sketch, "E1170.0", {"start": v(-562.61, -225.55) * mm, "end": v(-562.61, -258.32) * mm, "construction": true});
            skLineSegment(sketch, "E1171.0", {"start": v(-461.01, -225.55) * mm, "end": v(-461.01, -258.32) * mm, "construction": true});
            skLineSegment(sketch, "E1172.0", {"start": v(-461.01, -258.32) * mm, "end": v(-461.01, -287.78) * mm, "construction": true});
            skLineSegment(sketch, "E1173.0", {"start": v(-105.41, -258.32) * mm, "end": v(-105.41, -287.78) * mm, "construction": true});
            skLineSegment(sketch, "E1174.0", {"start": v(-105.41, -225.55) * mm, "end": v(-105.41, -258.32) * mm, "construction": true});
            skLineSegment(sketch, "E1175.0", {"start": v(-3.81, -225.55) * mm, "end": v(-3.81, -258.32) * mm, "construction": true});
            skLineSegment(sketch, "E1176.0", {"start": v(-3.81, -258.32) * mm, "end": v(-3.81, -287.78) * mm, "construction": true});
            skLineSegment(sketch, "E1177.0", {"start": v(351.8, -225.55) * mm, "end": v(351.8, -258.32) * mm, "construction": true});
            skLineSegment(sketch, "E1178.0", {"start": v(351.8, -258.32) * mm, "end": v(351.8, -287.78) * mm, "construction": true});
            skLineSegment(sketch, "E1179.0", {"start": v(453.4, -258.32) * mm, "end": v(453.4, -287.78) * mm, "construction": true});
            skLineSegment(sketch, "E1180.0", {"start": v(453.4, -225.55) * mm, "end": v(453.4, -258.32) * mm, "construction": true});
            skLineSegment(sketch, "E1181.0", {"start": v(478.8, -211.07) * mm, "end": v(478.8, -233.43) * mm, "construction": true});
            skLineSegment(sketch, "E1182.0", {"start": v(478.8, -233.43) * mm, "end": v(478.8, -262.13) * mm, "construction": true});
            skLineSegment(sketch, "E1183.0", {"start": v(478.8, -262.13) * mm, "end": v(478.8, -287.78) * mm, "construction": true});
            skLineSegment(sketch, "E1184.0", {"start": v(478.8, 300.48) * mm, "end": v(478.8, 391.41) * mm, "construction": true});
            skSolve(sketch);
        }
        {
            var Q0;
            Q0=qCreatedBy(makeId("Top.planeOp"),FACE);
            var sketch = newSketch(context, id + "F2", { "sketchPlane" : qUnion([Q0])});
            skLineSegment(sketch, "E1185", {"start": v(-584.83, 293.88) * mm, "end": v(-54.61, 293.88) * mm});
            skLineSegment(sketch, "E1186", {"start": v(-588.01, 290.7) * mm, "end": v(-588.01, 43.05) * mm});
            skPoint(sketch, "E1187", {"position": v(-582.44, -207.77) * mm});
            skPoint(sketch, "E1188.visualSharp", {"position": v(-588.01, 293.88) * mm});
            skArc(sketch, "E1188.filletArc", {"start": v(-584.83, 293.88) * mm, "mid": v(-587.08, 292.95) * mm, "end": v(-588.01, 290.7) * mm});
            skCircle(sketch, "E1189", {"center": v(-511.81, 268.48) * mm, "radius": 6.35 * mm});
            skCircle(sketch, "E1190", {"center": v(-562.61, -192.77) * mm, "radius": 6.35 * mm});
            skLineSegment(sketch, "E1191", {"start": v(-1059.64, 43.05) * mm, "end": v(610.48, 43.05) * mm, "construction": true});
            skLineSegment(sketch, "E1192.MirrorCS", {"start": v(-588.01, -204.6) * mm, "end": v(-588.01, 43.05) * mm});
            skArc(sketch, "E1193.MirrorCS", {"start": v(-584.83, -207.77) * mm, "mid": v(-587.08, -206.84) * mm, "end": v(-588.01, -204.6) * mm});
            skLineSegment(sketch, "E1194.MirrorCS", {"start": v(-584.83, -207.77) * mm, "end": v(-54.61, -207.77) * mm});
            skCircle(sketch, "E1195", {"center": v(-461.01, -192.77) * mm, "radius": 6.35 * mm});
            skCircle(sketch, "E1196", {"center": v(-105.41, -192.77) * mm, "radius": 6.35 * mm});
            skPoint(sketch, "E1197", {"position": v(-54.61, 274.83) * mm});
            skPoint(sketch, "E1198", {"position": v(-54.61, 262.13) * mm});
            skArc(sketch, "E1199", {"start": v(-54.56, 274.83) * mm, "mid": v(-60.96, 268.52) * mm, "end": v(-54.64, 262.13) * mm});
            skArc(sketch, "E1200", {"start": v(-54.64, 262.13) * mm, "mid": v(-48.26, 268.44) * mm, "end": v(-54.56, 274.83) * mm});
            skCircle(sketch, "E1201", {"center": v(-511.81, 268.48) * mm, "radius": 2.54 * mm});
            skCircle(sketch, "E1202", {"center": v(-562.61, -192.77) * mm, "radius": 2.54 * mm});
            skCircle(sketch, "E1203", {"center": v(-461.01, -192.77) * mm, "radius": 2.54 * mm});
            skCircle(sketch, "E1204", {"center": v(-105.41, -192.77) * mm, "radius": 2.54 * mm});
            skLineSegment(sketch, "E1205", {"start": v(-54.61, 279.3) * mm, "end": v(-54.61, 255.67) * mm, "construction": true});
            skPoint(sketch, "E1206", {"position": v(-54.61, 265.94) * mm});
            skPoint(sketch, "E1207", {"position": v(-54.61, 271.02) * mm});
            skArc(sketch, "E1208", {"start": v(-54.61, 271.02) * mm, "mid": v(-57.15, 268.48) * mm, "end": v(-54.61, 265.94) * mm});
            skArc(sketch, "E1209", {"start": v(-54.61, 265.94) * mm, "mid": v(-52.07, 268.48) * mm, "end": v(-54.61, 271.02) * mm});
            skArc(sketch, "E1210.MirrorCS", {"start": v(-54.61, 271.02) * mm, "mid": v(-52.07, 268.48) * mm, "end": v(-54.61, 265.94) * mm});
            skArc(sketch, "E1211.MirrorCS", {"start": v(-54.66, 274.83) * mm, "mid": v(-48.26, 268.52) * mm, "end": v(-54.58, 262.13) * mm});
            skLineSegment(sketch, "E1212.MirrorCS", {"start": v(475.6, 293.88) * mm, "end": v(-54.61, 293.88) * mm});
            skLineSegment(sketch, "E1213.MirrorCS", {"start": v(475.6, -207.77) * mm, "end": v(-54.61, -207.77) * mm});
            skArc(sketch, "E1214.MirrorCS", {"start": v(475.6, 293.88) * mm, "mid": v(477.86, 292.95) * mm, "end": v(478.79, 290.7) * mm});
            skArc(sketch, "E1215.MirrorCS", {"start": v(475.6, -207.77) * mm, "mid": v(477.86, -206.84) * mm, "end": v(478.79, -204.6) * mm});
            skCircle(sketch, "E1216.MirrorC", {"center": v(402.59, 268.48) * mm, "radius": 6.35 * mm});
            skCircle(sketch, "E1217.MirrorC", {"center": v(402.59, 268.48) * mm, "radius": 2.54 * mm});
            skCircle(sketch, "E1218.MirrorC", {"center": v(-3.81, -192.77) * mm, "radius": 2.54 * mm});
            skCircle(sketch, "E1219.MirrorC", {"center": v(351.79, -192.77) * mm, "radius": 2.54 * mm});
            skCircle(sketch, "E1220.MirrorC", {"center": v(453.39, -192.77) * mm, "radius": 2.54 * mm});
            skCircle(sketch, "E1221.MirrorC", {"center": v(453.39, -192.77) * mm, "radius": 6.35 * mm});
            skCircle(sketch, "E1222.MirrorC", {"center": v(351.79, -192.77) * mm, "radius": 6.35 * mm});
            skCircle(sketch, "E1223.MirrorC", {"center": v(-3.81, -192.77) * mm, "radius": 6.35 * mm});
            skPoint(sketch, "E1224.MirrorP", {"position": v(478.79, 293.88) * mm});
            skLineSegment(sketch, "E1225.MirrorCS", {"start": v(478.79, -204.6) * mm, "end": v(478.79, 43.05) * mm});
            skLineSegment(sketch, "E1226.MirrorCS", {"start": v(478.79, 290.7) * mm, "end": v(478.79, 43.05) * mm});
            skPoint(sketch, "E1227.MirrorP", {"position": v(473.22, -207.77) * mm});
            skSolve(sketch);
        }
        {
            var Q0;
            Q0=makeQuery(id+"F2.imprint","IMPRINT",FACE,{"disambiguationData":[TD([[makeQuery(id+"F2.imprint","IMPRINT",EDGE,{"derivedFrom":sQuery(id+"F2.wireOp",EDGE,"E1185")}),-1.0]])]});
            var Q1;
            Q1=makeQuery(id+"F2.imprint","IMPRINT",FACE,{"disambiguationData":[TD([[makeQuery(id+"F2.imprint","IMPRINT",EDGE,{"derivedFrom":sQuery(id+"F2.wireOp",EDGE,"E1189")}),1.0]])]});
            var Q2;
            Q2=makeQuery(id+"F2.imprint","IMPRINT",FACE,{"disambiguationData":[TD([[makeQuery(id+"F2.imprint","IMPRINT",EDGE,{"derivedFrom":sQuery(id+"F2.wireOp",EDGE,"E1199")}),1.0]])]});
            var Q3;
            Q3=makeQuery(id+"F2.imprint","IMPRINT",FACE,{"disambiguationData":[TD([[makeQuery(id+"F2.imprint","IMPRINT",EDGE,{"derivedFrom":sQuery(id+"F2.wireOp",EDGE,"E1216.MirrorC")}),-1.0]])]});
            var Q4;
            Q4=makeQuery(id+"F2.imprint","IMPRINT",FACE,{"disambiguationData":[TD([[makeQuery(id+"F2.imprint","IMPRINT",EDGE,{"derivedFrom":sQuery(id+"F2.wireOp",EDGE,"E1220.MirrorC")}),1.0]])]});
            var Q5;
            Q5=makeQuery(id+"F2.imprint","IMPRINT",FACE,{"disambiguationData":[TD([[makeQuery(id+"F2.imprint","IMPRINT",EDGE,{"derivedFrom":sQuery(id+"F2.wireOp",EDGE,"E1219.MirrorC")}),1.0]])]});
            var Q6;
            Q6=makeQuery(id+"F2.imprint","IMPRINT",FACE,{"disambiguationData":[TD([[makeQuery(id+"F2.imprint","IMPRINT",EDGE,{"derivedFrom":sQuery(id+"F2.wireOp",EDGE,"E1218.MirrorC")}),1.0]])]});
            var Q7;
            Q7=makeQuery(id+"F2.imprint","IMPRINT",FACE,{"disambiguationData":[TD([[makeQuery(id+"F2.imprint","IMPRINT",EDGE,{"derivedFrom":sQuery(id+"F2.wireOp",EDGE,"E1196")}),1.0]])]});
            var Q8;
            Q8=makeQuery(id+"F2.imprint","IMPRINT",FACE,{"disambiguationData":[TD([[makeQuery(id+"F2.imprint","IMPRINT",EDGE,{"derivedFrom":sQuery(id+"F2.wireOp",EDGE,"E1195")}),1.0]])]});
            var Q9;
            Q9=makeQuery(id+"F2.imprint","IMPRINT",FACE,{"disambiguationData":[TD([[makeQuery(id+"F2.imprint","IMPRINT",EDGE,{"derivedFrom":sQuery(id+"F2.wireOp",EDGE,"E1190")}),1.0]])]});
            extrude(context, id + "F3", {"entities" : qUnion([Q0, Q1, Q2, Q3, Q4, Q5, Q6, Q7, Q8, Q9]), "depth" : 19.05 * mm, "offsetDistance" : 25 * mm});
        }
        {
            var Q0;
            Q0=makeQuery(id+"F3.opExtrude","CAP_FACE",FACE,{"disambiguationData":[OSD([sQuery(id+"F2.wireOp",EDGE,"E1185"),sQuery(id+"F2.wireOp",EDGE,"E1186"),sQuery(id+"F2.wireOp",EDGE,"E1188.filletArc"),sQuery(id+"F2.wireOp",EDGE,"E1192.MirrorCS"),sQuery(id+"F2.wireOp",EDGE,"E1193.MirrorCS"),sQuery(id+"F2.wireOp",EDGE,"E1194.MirrorCS"),sQuery(id+"F2.wireOp",EDGE,"E1201"),sQuery(id+"F2.wireOp",EDGE,"E1202"),sQuery(id+"F2.wireOp",EDGE,"E1203"),sQuery(id+"F2.wireOp",EDGE,"E1204"),sQuery(id+"F2.wireOp",EDGE,"E1208"),sQuery(id+"F2.wireOp",EDGE,"E1210.MirrorCS"),sQuery(id+"F2.wireOp",EDGE,"E1212.MirrorCS"),sQuery(id+"F2.wireOp",EDGE,"E1213.MirrorCS"),sQuery(id+"F2.wireOp",EDGE,"E1214.MirrorCS"),sQuery(id+"F2.wireOp",EDGE,"E1215.MirrorCS"),sQuery(id+"F2.wireOp",EDGE,"E1217.MirrorC"),sQuery(id+"F2.wireOp",EDGE,"E1218.MirrorC"),sQuery(id+"F2.wireOp",EDGE,"E1219.MirrorC"),sQuery(id+"F2.wireOp",EDGE,"E1220.MirrorC"),sQuery(id+"F2.wireOp",EDGE,"E1225.MirrorCS"),sQuery(id+"F2.wireOp",EDGE,"E1226.MirrorCS")])],"isStart":false});
            var sketch = newSketch(context, id + "F4", { "sketchPlane" : qUnion([Q0])});
            skCircle(sketch, "E1228.0", {"center": v(-511.81, 268.48) * mm, "radius": 6.35 * mm});
            skArc(sketch, "E1229.0", {"start": v(-54.64, 262.13) * mm, "mid": v(-48.26, 268.44) * mm, "end": v(-54.56, 274.83) * mm});
            skArc(sketch, "E1230.0", {"start": v(-54.56, 274.83) * mm, "mid": v(-60.96, 268.52) * mm, "end": v(-54.64, 262.13) * mm});
            skCircle(sketch, "E1231.0", {"center": v(402.59, 268.48) * mm, "radius": 6.35 * mm});
            skCircle(sketch, "E1232.0", {"center": v(453.39, -192.77) * mm, "radius": 6.35 * mm});
            skCircle(sketch, "E1233.0", {"center": v(351.79, -192.77) * mm, "radius": 6.35 * mm});
            skCircle(sketch, "E1234.0", {"center": v(-3.81, -192.77) * mm, "radius": 6.35 * mm});
            skCircle(sketch, "E1235.0", {"center": v(-105.41, -192.77) * mm, "radius": 6.35 * mm});
            skCircle(sketch, "E1236.0", {"center": v(-461.01, -192.77) * mm, "radius": 6.35 * mm});
            skCircle(sketch, "E1237.0", {"center": v(-562.61, -192.77) * mm, "radius": 6.35 * mm});
            skSolve(sketch);
        }
        {
            var Q0;
            Q0 = qSketchRegion(id + "F4", true);
            extrude(context, id + "F5", {"entities" : qUnion([Q0]), "operationType" : NewBodyOperationType.REMOVE, "oppositeDirection" : true, "depth" : 6.35 * mm, "offsetDistance" : 25 * mm});
        }
    });
